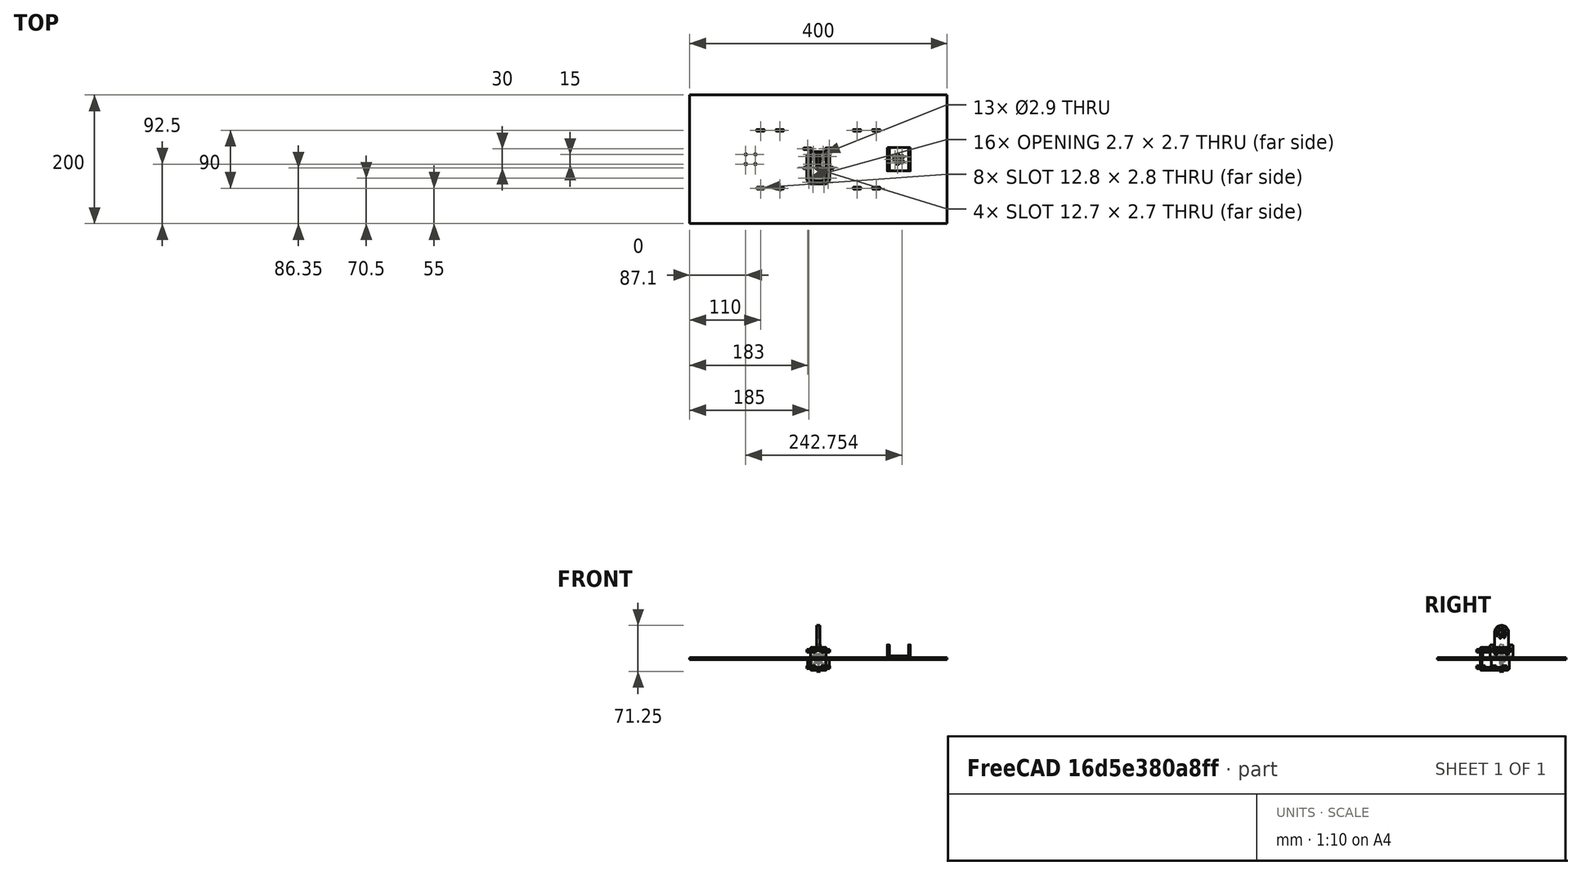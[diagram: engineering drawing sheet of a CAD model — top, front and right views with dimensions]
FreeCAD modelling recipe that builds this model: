
FCSTD DOCUMENT  (FreeCAD 1.1R20260414 (Git shallow))
Label: Unnamed
License: All rights reserved
LicenseURL: https://en.wikipedia.org/wiki/All_rights_reserved
objects: Sketcher::SketchObject×15, App::Point×8, App::Link×8, App::FeaturePython×8, PartDesign::Hole×7, Part::Feature×7, PartDesign::Pad×6, App::Part×4, PartDesign::Mirrored×3, PartDesign::Fillet×3, PartDesign::Body×3, PartDesign::Pocket×2, PartDesign::PolarPattern×2, TechDraw::DrawViewDimension×2, PartDesign::ShapeBinder×1, Assembly::JointGroup×1, Assembly::AssemblyObject×1, TechDraw::DrawSVGTemplate×1, TechDraw::DrawProjGroupItem×1, TechDraw::DrawPage×1
note: 107 computed .brp shape members not serialized (recipe doc carries the construction recipe); baked Part::Feature solids carry a one-line shape summary decoded from their .brp
EXTERNAL_REF file=Unnamed1.FCStd obj=Body

FEATURE [App::Point] Origin001
  Role = Origin
FEATURE [Sketcher::SketchObject] Sketch
  ArcFitTolerance = 1e-06
  AttachmentSupport = -> [Origin]
  ExternalTypes = [0]
  FullyConstrained = true
  MakeInternals = false
  MapMode = 5
  _ExternalGeoVersion = 1
  sketch-geometry (5):
    g0: LineSegment StartX=-200 StartY=-100 StartZ=0 EndX=200 EndY=-100 EndZ=0
    g1: LineSegment StartX=200 StartY=-100 StartZ=0 EndX=200 EndY=100 EndZ=0
    g2: LineSegment StartX=200 StartY=100 StartZ=0 EndX=-200 EndY=100 EndZ=0
    g3: LineSegment StartX=-200 StartY=100 StartZ=0 EndX=-200 EndY=-100 EndZ=0
    g4: GeomPoint [constr] X=0 Y=0 Z=0
  constraints (12):
    c: Coincident(g0,g1)
    c: Coincident(g1,g2)
    c: Coincident(g2,g3)
    c: Coincident(g3,g0)
    c: Horizontal(g0)
    c: Horizontal(g2)
    c: Vertical(g1)
    c: Vertical(g3)
    c: Symmetric(g2,g0,g4)
    c: Distance(g1,g3) = 400
    c: Distance(g0,g2) = 200
    c: Coincident(g4,g-1)
FEATURE [PartDesign::Pad] Pad
  Direction = (0,0,1)
  Length = 3
  Length2 = 10
  Profile = -> Sketch
  ReferenceAxis = -> Sketch [N_Axis]
  Refine = true
  SideType = 0
  Suppressed = false
  Type = 0
  Type2 = 0
FEATURE [Sketcher::SketchObject] Sketch001
  ArcFitTolerance = 1e-06
  AttachmentSupport = -> [Pad]
  ExternalTypes = [0]
  FullyConstrained = true
  MakeInternals = false
  MapMode = 5
  Placement = pos=(0,0,3) rot=(0,0,1;0rad)
  _ExternalGeoVersion = 1
  sketch-geometry (16):
    g0: ArcOfCircle CenterX=-12 CenterY=16.35 CenterZ=0 NormalX=0 NormalY=0 NormalZ=1 AngleXU=0 Radius=1.35 StartAngle=4.71239 EndAngle=7.85398
    g1: ArcOfCircle CenterX=-22 CenterY=16.35 CenterZ=0 NormalX=0 NormalY=0 NormalZ=1 AngleXU=0 Radius=1.35 StartAngle=1.5708 EndAngle=4.71239
    g2: LineSegment StartX=-12 StartY=15 StartZ=0 EndX=-22 EndY=15 EndZ=0
    g3: LineSegment StartX=-12 StartY=17.7 StartZ=0 EndX=-22 EndY=17.7 EndZ=0
    g4: ArcOfCircle CenterX=12 CenterY=16.35 CenterZ=0 NormalX=0 NormalY=0 NormalZ=1 AngleXU=0 Radius=1.35 StartAngle=1.5708 EndAngle=4.71239
    g5: ArcOfCircle CenterX=22 CenterY=16.35 CenterZ=0 NormalX=0 NormalY=0 NormalZ=1 AngleXU=0 Radius=1.35 StartAngle=4.71239 EndAngle=7.85398
    g6: LineSegment StartX=12 StartY=17.7 StartZ=0 EndX=22 EndY=17.7 EndZ=0
    g7: LineSegment StartX=12 StartY=15 StartZ=0 EndX=22 EndY=15 EndZ=0
    g8: ArcOfCircle CenterX=-22 CenterY=-13.65 CenterZ=0 NormalX=0 NormalY=0 NormalZ=1 AngleXU=0 Radius=1.35 StartAngle=1.5708 EndAngle=4.71239
    g9: ArcOfCircle CenterX=-12 CenterY=-13.65 CenterZ=0 NormalX=0 NormalY=0 NormalZ=1 AngleXU=0 Radius=1.35 StartAngle=4.71239 EndAngle=7.85398
    g10: LineSegment StartX=-22 StartY=-12.3 StartZ=0 EndX=-12 EndY=-12.3 EndZ=0
    g11: LineSegment StartX=-22 StartY=-15 StartZ=0 EndX=-12 EndY=-15 EndZ=0
    g12: ArcOfCircle CenterX=12 CenterY=-13.65 CenterZ=0 NormalX=0 NormalY=0 NormalZ=1 AngleXU=0 Radius=1.35 StartAngle=1.5708 EndAngle=4.71239
    g13: ArcOfCircle CenterX=22 CenterY=-13.65 CenterZ=0 NormalX=0 NormalY=0 NormalZ=1 AngleXU=0 Radius=1.35 StartAngle=4.71239 EndAngle=7.85398
    g14: LineSegment StartX=12 StartY=-12.3 StartZ=0 EndX=22 EndY=-12.3 EndZ=0
    g15: LineSegment StartX=12 StartY=-15 StartZ=0 EndX=22 EndY=-15 EndZ=0
  constraints (40):
    c: Tangent(g0,g2) = 1.5708
    c: Tangent(g0,g3) = -1.5708
    c: Tangent(g1,g2) = 1.5708
    c: Tangent(g1,g3) = -1.5708
    c: Equal(g0,g1)
    c: Distance(g0,g1) = 10
    c: Radius(g0) = 1.35
    c: Horizontal(g2)
    c: Distance(g0,g-2) = 12
    c: Tangent(g4,g6) = 1.5708
    c: Tangent(g4,g7) = -1.5708
    c: Tangent(g5,g6) = 1.5708
    c: Tangent(g5,g7) = -1.5708
    c: Equal(g4,g5)
    c: Distance(g4,g5) = 10
    c: Radius(g4) = 1.35
    c: Horizontal(g6)
    c: Distance(g4,g-2) = 12
    c: Distance(g-1,g7) = 15
    c: Distance(g-1,g2) = 15
    c: Tangent(g8,g10) = 1.5708
    c: Tangent(g8,g11) = -1.5708
    c: Tangent(g9,g10) = 1.5708
    c: Tangent(g9,g11) = -1.5708
    c: Equal(g8,g9)
    c: Distance(g8,g9) = 10
    c: Radius(g8) = 1.35
    c: Horizontal(g10)
    c: Distance(g9,g-2) = 12
    c: DistanceY(g9,g0) = 30
    c: Tangent(g12,g14) = 1.5708
    c: Tangent(g12,g15) = -1.5708
    c: Tangent(g13,g14) = 1.5708
    c: Tangent(g13,g15) = -1.5708
    c: Equal(g12,g13)
    c: Distance(g12,g13) = 10
    c: Radius(g12) = 1.35
    c: Horizontal(g14)
    c: Distance(g12,g-2) = 12
    c: Distance(g12,g4) = 30
FEATURE [PartDesign::Pocket] Pocket
  BaseFeature = -> Pad
  Direction = (0,0,-1)
  Length = 5
  Length2 = 5
  Profile = -> Sketch001
  ReferenceAxis = -> Sketch001 [N_Axis]
  Refine = true
  SideType = 0
  Suppressed = false
  Type = 0
  Type2 = 0
FEATURE [Sketcher::SketchObject] Sketch002
  ArcFitTolerance = 1e-06
  AttachmentSupport = -> [Pocket]
  ExternalTypes = [0]
  FullyConstrained = true
  MakeInternals = false
  MapMode = 5
  Placement = pos=(0,0,3) rot=(0,0,1;0rad)
  _ExternalGeoVersion = 1
  sketch-geometry (8):
    g0: ArcOfCircle CenterX=-55 CenterY=-45 CenterZ=0 NormalX=0 NormalY=0 NormalZ=1 AngleXU=0 Radius=1.4 StartAngle=4.71239 EndAngle=7.85398
    g1: ArcOfCircle CenterX=-65 CenterY=-45 CenterZ=0 NormalX=0 NormalY=0 NormalZ=1 AngleXU=0 Radius=1.4 StartAngle=1.5708 EndAngle=4.71239
    g2: LineSegment StartX=-55 StartY=-46.4 StartZ=0 EndX=-65 EndY=-46.4 EndZ=0
    g3: LineSegment StartX=-55 StartY=-43.6 StartZ=0 EndX=-65 EndY=-43.6 EndZ=0
    g4: ArcOfCircle CenterX=-85 CenterY=-45 CenterZ=0 NormalX=0 NormalY=0 NormalZ=1 AngleXU=0 Radius=1.4 StartAngle=4.71239 EndAngle=7.85398
    g5: ArcOfCircle CenterX=-95 CenterY=-45 CenterZ=0 NormalX=0 NormalY=0 NormalZ=1 AngleXU=0 Radius=1.4 StartAngle=1.5708 EndAngle=4.71239
    g6: LineSegment StartX=-85 StartY=-46.4 StartZ=0 EndX=-95 EndY=-46.4 EndZ=0
    g7: LineSegment StartX=-85 StartY=-43.6 StartZ=0 EndX=-95 EndY=-43.6 EndZ=0
  constraints (20):
    c: Tangent(g0,g2) = 1.5708
    c: Tangent(g0,g3) = -1.5708
    c: Tangent(g1,g2) = 1.5708
    c: Tangent(g1,g3) = -1.5708
    c: Equal(g0,g1)
    c: Distance(g0,g1) = 10
    c: Radius(g0) = 1.4
    c: Horizontal(g2)
    c: Distance(g0,g-2) = 55
    c: Distance(g0,g-1) = 45
    c: Tangent(g4,g6) = 1.5708
    c: Tangent(g4,g7) = -1.5708
    c: Tangent(g5,g6) = 1.5708
    c: Tangent(g5,g7) = -1.5708
    c: Equal(g4,g5)
    c: Distance(g4,g5) = 10
    c: Radius(g4) = 1.4
    c: Horizontal(g6)
    c: DistanceX(g4,g1) = 20
    c: Distance(g5,g-1) = 45
FEATURE [PartDesign::Pocket] Pocket001
  BaseFeature = -> Pocket
  Direction = (0,0,-1)
  Length = 5
  Length2 = 5
  Profile = -> Sketch002
  ReferenceAxis = -> Sketch002 [N_Axis]
  Refine = true
  SideType = 0
  Suppressed = false
  Type = 0
  Type2 = 0
FEATURE [PartDesign::Mirrored] Mirrored
  BaseFeature = -> Pocket001
  MirrorPlane = -> Sketch002 [V_Axis]
  Originals = -> [Pocket001]
  Refine = true
  Suppressed = false
  TransformMode = 0
FEATURE [PartDesign::Mirrored] Mirrored001
  BaseFeature = -> Mirrored
  MirrorPlane = -> Sketch002 [H_Axis]
  Originals = -> [Pocket001]
  Refine = true
  Suppressed = false
  TransformMode = 0
FEATURE [PartDesign::PolarPattern] PolarPattern
  Angle = 360
  Axis = -> Sketch002 [N_Axis]
  BaseFeature = -> Mirrored001
  Mode = 0
  Occurrences = 2
  Offset = 120
  Originals = -> [Pocket001]
  Refine = true
  SpacingPattern = [0]
  Spacings = [-1]
  Suppressed = false
  TransformMode = 0
FEATURE [PartDesign::ShapeBinder] CopyPart__Feature
  TraceSupport = false
FEATURE [Sketcher::SketchObject] Sketch003
  ArcFitTolerance = 1e-06
  AttachmentSupport = -> [CopyPart__Feature]
  ExternalTypes = [0]
  FullyConstrained = true
  MakeInternals = false
  MapMode = 5
  Placement = pos=(0,-38.6,0) rot=(1,0,0;1.5708rad)
  _ExternalGeoVersion = 1
  sketch-geometry (5):
    g0: LineSegment StartX=-18 StartY=-15 StartZ=0 EndX=18 EndY=-15 EndZ=0
    g1: LineSegment StartX=18 StartY=-15 StartZ=0 EndX=18 EndY=15 EndZ=0
    g2: LineSegment StartX=18 StartY=15 StartZ=0 EndX=-18 EndY=15 EndZ=0
    g3: LineSegment StartX=-18 StartY=15 StartZ=0 EndX=-18 EndY=-15 EndZ=0
    g4: GeomPoint [constr] X=0 Y=0 Z=0
  constraints (12):
    c: Coincident(g0,g1)
    c: Coincident(g1,g2)
    c: Coincident(g2,g3)
    c: Coincident(g3,g0)
    c: Horizontal(g0)
    c: Horizontal(g2)
    c: Vertical(g1)
    c: Vertical(g3)
    c: Symmetric(g2,g0,g4)
    c: Distance(g1,g3) = 36
    c: Distance(g0,g2) = 30
    c: Coincident(g4,g-1)
FEATURE [PartDesign::Pad] Pad001
  Direction = (0,-1,2e-16)
  Length = 3
  Length2 = 10
  Profile = -> Sketch003
  ReferenceAxis = -> Sketch003 [N_Axis]
  Refine = true
  SideType = 0
  Suppressed = false
  Type = 0
  Type2 = 0
FEATURE [Sketcher::SketchObject] Sketch004
  ArcFitTolerance = 1e-06
  AttachmentSupport = -> [Pad001]
  ExternalTypes = [0]
  FullyConstrained = true
  MakeInternals = false
  MapMode = 5
  Placement = pos=(0,3.3e-15,15) rot=(0,0,1;0rad)
  _ExternalGeoVersion = 1
  sketch-geometry (12):
    g0: LineSegment StartX=-18 StartY=-21.6 StartZ=0 EndX=-12.5 EndY=-21.6 EndZ=0
    g1: LineSegment StartX=-12.5 StartY=-21.6 StartZ=0 EndX=-12.5 EndY=-33.6 EndZ=0
    g2: LineSegment StartX=-12.5 StartY=-33.6 StartZ=0 EndX=12.5 EndY=-33.6 EndZ=0
    g3: LineSegment StartX=12.5 StartY=-33.6 StartZ=0 EndX=12.5 EndY=-21.6 EndZ=0
    g4: LineSegment StartX=12.5 StartY=-21.6 StartZ=0 EndX=18 EndY=-21.6 EndZ=0
    g5: LineSegment StartX=18 StartY=-21.6 StartZ=0 EndX=18 EndY=-41.6 EndZ=0
    g6: LineSegment StartX=18 StartY=-41.6 StartZ=0 EndX=-18 EndY=-41.6 EndZ=0
    g7: LineSegment StartX=-18 StartY=-41.6 StartZ=0 EndX=-18 EndY=-21.6 EndZ=0
    g8: Circle CenterX=-15 CenterY=-29.5 CenterZ=0 NormalX=0 NormalY=0 NormalZ=1 AngleXU=0 Radius=1.5
    g9: Circle CenterX=-8.5 CenterY=-35.8 CenterZ=0 NormalX=0 NormalY=0 NormalZ=1 AngleXU=0 Radius=1.5
    g10: Circle CenterX=8.5 CenterY=-35.8 CenterZ=0 NormalX=0 NormalY=0 NormalZ=1 AngleXU=0 Radius=1.5
    g11: Circle CenterX=15 CenterY=-29.5 CenterZ=0 NormalX=0 NormalY=0 NormalZ=1 AngleXU=0 Radius=1.5
  constraints (36):
    c: Horizontal(g0)
    c: Coincident(g0,g1)
    c: Vertical(g1)
    c: Coincident(g1,g2)
    c: Horizontal(g2)
    c: Coincident(g2,g3)
    c: Vertical(g3)
    c: Coincident(g3,g4)
    c: Horizontal(g4)
    c: Coincident(g4,g5)
    c: Vertical(g5)
    c: Coincident(g5,g6)
    c: Horizontal(g6)
    c: Coincident(g6,g7)
    c: Coincident(g7,g0)
    c: Vertical(g7)
    c: DistanceX(g6,g6) = 36
    c: DistanceY(g7,g7) = 20
    c: Distance(g3,g1) = 25
    c: Equal(g0,g4)
    c: Equal(g3,g1)
    c: Distance(g-1,g6) = 41.6
    c: Distance(g-2,g7) = 18
    c: Distance(g6,g2) = 8
    c: Diameter(g8) = 3
    c: Equal(g8,g9)
    c: Equal(g9,g10)
    c: Equal(g10,g11)
    c: Distance(g8,g7) = 3
    c: Distance(g9,g6) = 5.8
    c: Distance(g9,g7) = 9.5
    c: Distance(g10,g5) = 9.5
    c: Distance(g10,g6) = 5.8
    c: Distance(g11,g5) = 3
    c: Distance(g8,g0) = 7.9
    c: Distance(g11,g4) = 7.9
FEATURE [PartDesign::Pad] Pad002
  BaseFeature = -> Pad001
  Direction = (0,0,1)
  Length = 3
  Length2 = 10
  Profile = -> Sketch004
  ReferenceAxis = -> Sketch004 [N_Axis]
  Refine = true
  SideType = 0
  Suppressed = false
  Type = 0
  Type2 = 0
FEATURE [PartDesign::Mirrored] Mirrored002
  BaseFeature = -> Pad002
  MirrorPlane = -> XY_Plane001
  Originals = -> [Pad002]
  Refine = true
  Suppressed = false
  TransformMode = 0
FEATURE [PartDesign::Fillet] Fillet001
  Base = -> Mirrored002 [Edge60,Edge47,Edge36,Edge27]
  BaseFeature = -> Mirrored002
  Radius = 2
  Refine = true
  SupportTransform = false
  Suppressed = false
  UseAllEdges = false
FEATURE [PartDesign::Fillet] Fillet002
  Base = -> Fillet001 [Edge51,Edge56]
  BaseFeature = -> Fillet001
  Radius = 1
  Refine = true
  SupportTransform = false
  Suppressed = false
  UseAllEdges = false
FEATURE [Sketcher::SketchObject] Sketch005
  ArcFitTolerance = 1e-06
  AttachmentSupport = -> [Fillet002]
  ExternalTypes = [0]
  FullyConstrained = true
  MakeInternals = false
  MapMode = 5
  Placement = pos=(0,-38.6,0) rot=(0,0.707107,0.707107;3.14159rad)
  _ExternalGeoVersion = 1
  sketch-geometry (1):
    g0: Circle CenterX=0 CenterY=6 CenterZ=0 NormalX=0 NormalY=0 NormalZ=1 AngleXU=0 Radius=1.25
  constraints (3):
    c: Diameter(g0) = 2.5
    c: PointOnObject(g0,g-2)
    c: Distance(g0,g-1) = 6
FEATURE [PartDesign::Hole] Hole
  BaseFeature = -> Fillet002
  BaseProfileType = 7
  CustomThreadClearance = 0
  Depth = 5
  DepthType = 0
  Diameter = 2.9
  DrillForDepth = false
  DrillPoint = 1
  DrillPointAngle = 118
  HoleCutCountersinkAngle = 90
  HoleCutCustomValues = false
  HoleCutDepth = 2.65
  HoleCutDiameter = 5.3
  HoleCutType = 7
  ModelThread = false
  Profile = -> Sketch005
  Refine = true
  Suppressed = false
  Tapered = false
  TaperedAngle = 90
  ThreadClass = 0
  ThreadDepth = 5
  ThreadDepthType = 0
  ThreadDiameter = 2.5
  ThreadDirection = 0
  ThreadFit = 0
  ThreadSize = 8
  ThreadType = 1
  Threaded = false
  UseCustomThreadClearance = false
FEATURE [PartDesign::PolarPattern] PolarPattern001
  Angle = 360
  Axis = -> Sketch005 [N_Axis]
  BaseFeature = -> Hole
  Mode = 0
  Occurrences = 5
  Offset = 120
  Originals = -> [Hole]
  Refine = true
  SpacingPattern = [0]
  Spacings = [-1,-1,-1,-1]
  Suppressed = false
  TransformMode = 0
FEATURE [App::Point] Origin003
  Role = Origin
FEATURE [PartDesign::Body] Body001  label="mx_28_holder"
  AllowCompound = true
  Group = -> [CopyPart__Feature,Sketch003,Pad001,Sketch004,Pad002,Mirrored002,Fillet001,Fillet002,Sketch005,Hole,PolarPattern001]
  Origin = -> Origin002
  Placement = pos=(125,5.4e-15,44.5) rot=(-0.57735,0.57735,0.57735;4.18879rad)
  Tip = -> PolarPattern001
FEATURE [App::Point] Origin006  label="Origin008"
  Role = Origin
FEATURE [Part::Feature] Part__Feature  label="DC07_00A_DUMMY_NONE"
  Placement = pos=(0,0,1) rot=(0,0,1;0rad)
  shape: bbox 35.6 x 51.12 x 41.85 mm, 333 faces (baked)
FEATURE [App::Point] Origin008  label="Origin010"
  Role = Origin
FEATURE [Part::Feature] Part__Feature001  label="SOLID001"
  shape: bbox 22 x 3.05 x 22 mm, 56 faces (baked)
FEATURE [Part::Feature] Part__Feature002  label="COMPOUND001"
  shape: bbox 18 x 1.95 x 18 mm, 16 faces, 0 solids (baked)
FEATURE [App::Part] HN07_I_02
  Group = -> [Part__Feature001,Part__Feature002]
  Origin = -> Origin009
  Placement = pos=(2e-16,0,-19.15) rot=(-0.672416,0.523382,-0.523382;1.95765rad)
FEATURE [App::Point] Origin010  label="Origin012"
  Role = Origin
FEATURE [Part::Feature] Part__Feature003  label="SOLID"
  shape: bbox 22 x 5.851 x 22 mm, 149 faces (baked)
FEATURE [Part::Feature] Part__Feature004  label="COMPOUND"
  shape: bbox 18 x 1.95 x 18 mm, 16 faces, 0 solids (baked)
FEATURE [App::Part] HN07_N_02
  Group = -> [Part__Feature003,Part__Feature004]
  Origin = -> Origin011
  Placement = pos=(0,0,19.3) rot=(0.57735,0.57735,0.57735;2.0944rad)
FEATURE [App::Part] Unnamed  label="mx28"
  Group = -> [Part__Feature,HN07_I_02,HN07_N_02]
  Origin = -> Origin007
  Placement = pos=(126,-4.25e-14,45) rot=(0.57735,-0.57735,-0.57735;2.0944rad)
FEATURE [Sketcher::SketchObject] Sketch006
  ArcFitTolerance = 1e-06
  AttachmentSupport = -> [PolarPattern]
  ExternalTypes = [0]
  FullyConstrained = true
  MakeInternals = false
  MapMode = 5
  Placement = pos=(0,0,3) rot=(0,0,1;0rad)
  _ExternalGeoVersion = 1
  sketch-geometry (5):
    g0: Circle CenterX=123.15 CenterY=5.7 CenterZ=0 NormalX=0 NormalY=0 NormalZ=1 AngleXU=0 Radius=1.25
    g1: Circle CenterX=119 CenterY=0 CenterZ=0 NormalX=0 NormalY=0 NormalZ=1 AngleXU=0 Radius=1.25
    g2: Circle CenterX=129.85 CenterY=3.55 CenterZ=0 NormalX=0 NormalY=0 NormalZ=1 AngleXU=0 Radius=1.25
    g3: Circle CenterX=123.15 CenterY=-5.7 CenterZ=0 NormalX=0 NormalY=0 NormalZ=1 AngleXU=0 Radius=1.25
    g4: Circle CenterX=129.85 CenterY=-3.52 CenterZ=0 NormalX=0 NormalY=0 NormalZ=1 AngleXU=0 Radius=1.25
  constraints (15):
    c: Diameter(g0) = 2.5
    c: PointOnObject(g1,g-1)
    c: Equal(g1,g0)
    c: Equal(g1,g3)
    c: Equal(g3,g4)
    c: Equal(g4,g2)
    c: DistanceX(g-1,g0) = 123.15
    c: DistanceX(g-1,g1) = 119
    c: DistanceX(g-1,g3) = 123.15
    c: DistanceX(g-1,g4) = 129.85
    c: DistanceX(g-1,g2) = 129.85
    c: Distance(g0,g-1) = 5.7
    c: Distance(g2,g-1) = 3.55
    c: Distance(g4,g-1) = 3.52
    c: Distance(g3,g-1) = 5.7
FEATURE [PartDesign::Hole] Hole001
  BaseFeature = -> PolarPattern
  BaseProfileType = 7
  CustomThreadClearance = 0
  Depth = 5
  DepthType = 0
  Diameter = 3.1
  DrillForDepth = false
  DrillPoint = 1
  DrillPointAngle = 118
  HoleCutCountersinkAngle = 90
  HoleCutCustomValues = false
  HoleCutDepth = 0
  HoleCutDiameter = 0
  HoleCutType = 0
  ModelThread = false
  Profile = -> Sketch006
  Refine = true
  Suppressed = false
  Tapered = false
  TaperedAngle = 90
  ThreadClass = 0
  ThreadDepth = 5
  ThreadDepthType = 0
  ThreadDiameter = 2.5
  ThreadDirection = 0
  ThreadFit = 2
  ThreadSize = 8
  ThreadType = 1
  Threaded = false
  UseCustomThreadClearance = false
FEATURE [Sketcher::SketchObject] Sketch011
  ArcFitTolerance = 1e-06
  AttachmentSupport = -> [Hole001]
  ExternalTypes = [0]
  FullyConstrained = true
  MakeInternals = false
  MapMode = 5
  Placement = pos=(0,0,3) rot=(0,0,1;0rad)
  _ExternalGeoVersion = 1
  sketch-geometry (5):
    g0: GeomPoint [constr] X=-105.4 Y=0 Z=0
    g1: Circle CenterX=-97.9 CenterY=7.49998 CenterZ=0 NormalX=0 NormalY=0 NormalZ=1 AngleXU=0 Radius=1.1
    g2: Circle CenterX=-112.9 CenterY=7.50002 CenterZ=0 NormalX=0 NormalY=0 NormalZ=1 AngleXU=0 Radius=1.1
    g3: Circle CenterX=-112.9 CenterY=-7.49998 CenterZ=0 NormalX=0 NormalY=0 NormalZ=1 AngleXU=0 Radius=1.1
    g4: Circle CenterX=-97.9 CenterY=-7.50002 CenterZ=0 NormalX=0 NormalY=0 NormalZ=1 AngleXU=0 Radius=1.1
  constraints (13):
    c: PointOnObject(g0,g-1)
    c: Symmetric(g1,g3,g0)
    c: Distance(g4,g3) = 15
    c: Distance(g3,g2) = 15
    c: Diameter(g1) = 2.2
    c: Equal(g1,g2)
    c: Equal(g2,g3)
    c: Equal(g3,g4)
    c: DistanceX(g1,g-1) = 97.9
    c: Distance(g1,g4) = 15
    c: DistanceX(g2,g1) = 15
    c: DistanceX(g3,g-1) = 112.9
    c: DistanceX(g4,g-1) = 97.9
FEATURE [PartDesign::Hole] Hole004
  BaseFeature = -> Hole001
  BaseProfileType = 7
  CustomThreadClearance = 0
  Depth = 5
  DepthType = 0
  Diameter = 2.9
  DrillForDepth = false
  DrillPoint = 1
  DrillPointAngle = 118
  HoleCutCountersinkAngle = 90
  HoleCutCustomValues = false
  HoleCutDepth = 0
  HoleCutDiameter = 0
  HoleCutType = 0
  ModelThread = false
  Profile = -> Sketch011
  Refine = true
  Suppressed = false
  Tapered = false
  TaperedAngle = 90
  ThreadClass = 0
  ThreadDepth = 5
  ThreadDepthType = 0
  ThreadDiameter = 2.5
  ThreadDirection = 0
  ThreadFit = 0
  ThreadSize = 8
  ThreadType = 1
  Threaded = false
  UseCustomThreadClearance = false
FEATURE [PartDesign::Body] Body  label="base"
  AllowCompound = true
  Group = -> [Sketch,Pad,Sketch001,Pocket,Sketch002,Pocket001,Mirrored,Mirrored001,PolarPattern,Sketch006,Hole001,Sketch011,Hole004]
  Origin = -> Origin
  Tip = -> Hole004
FEATURE [App::Point] Origin014  label="Origin016"
  Role = Origin
FEATURE [Part::Feature] Part__Feature005  label="SOLID002"
  shape: bbox 22 x 3.05 x 22 mm, 56 faces (baked)
FEATURE [Part::Feature] Part__Feature006  label="COMPOUND002"
  shape: bbox 18 x 1.95 x 18 mm, 16 faces, 0 solids (baked)
FEATURE [App::Part] HN07_I_001
  Group = -> [Part__Feature005,Part__Feature006]
  Origin = -> Origin015
  Placement = pos=(-102.51,0.0161296,44.95) rot=(-0.702206,0.711974,0;3.14159rad)
FEATURE [App::Point] Origin012  label="Origin014"
  Role = Origin
FEATURE [Sketcher::SketchObject] Sketch012
  ArcFitTolerance = 1e-06
  AttachmentSupport = -> [Origin013]
  ExternalTypes = [0]
  FullyConstrained = true
  MakeInternals = false
  MapMode = 5
  _ExternalGeoVersion = 1
  sketch-geometry (5):
    g0: LineSegment StartX=-12 StartY=-12 StartZ=0 EndX=12 EndY=-12 EndZ=0
    g1: LineSegment StartX=12 StartY=-12 StartZ=0 EndX=12 EndY=12 EndZ=0
    g2: LineSegment StartX=12 StartY=12 StartZ=0 EndX=-12 EndY=12 EndZ=0
    g3: LineSegment StartX=-12 StartY=12 StartZ=0 EndX=-12 EndY=-12 EndZ=0
    g4: GeomPoint [constr] X=0 Y=0 Z=0
  constraints (12):
    c: Coincident(g0,g1)
    c: Coincident(g1,g2)
    c: Coincident(g2,g3)
    c: Coincident(g3,g0)
    c: Horizontal(g0)
    c: Horizontal(g2)
    c: Vertical(g1)
    c: Vertical(g3)
    c: Symmetric(g2,g0,g4)
    c: Distance(g1,g3) = 24
    c: Distance(g0,g2) = 24
    c: Coincident(g4,g-1)
FEATURE [PartDesign::Pad] Pad003
  Direction = (0,0,1)
  Length = 5
  Length2 = 10
  Profile = -> Sketch012
  ReferenceAxis = -> Sketch012 [N_Axis]
  Refine = true
  SideType = 0
  Suppressed = false
  Type = 0
  Type2 = 0
FEATURE [Sketcher::SketchObject] Sketch013
  ArcFitTolerance = 1e-06
  AttachmentSupport = -> [Pad003]
  ExternalTypes = [0]
  FullyConstrained = true
  MakeInternals = false
  MapMode = 5
  Placement = pos=(0,0,5) rot=(0,0,1;0rad)
  _ExternalGeoVersion = 1
  sketch-geometry (5):
    g0: GeomPoint [constr] X=0 Y=0 Z=0
    g1: Circle CenterX=7.5 CenterY=7.5 CenterZ=0 NormalX=0 NormalY=0 NormalZ=1 AngleXU=0 Radius=1.1
    g2: Circle CenterX=-7.5 CenterY=7.5 CenterZ=0 NormalX=0 NormalY=0 NormalZ=1 AngleXU=0 Radius=1.1
    g3: Circle CenterX=-7.5 CenterY=-7.5 CenterZ=0 NormalX=0 NormalY=0 NormalZ=1 AngleXU=0 Radius=1.1
    g4: Circle CenterX=7.5 CenterY=-7.5 CenterZ=0 NormalX=0 NormalY=0 NormalZ=1 AngleXU=0 Radius=1.1
  constraints (12):
    c: Symmetric(g1,g3,g0)
    c: Distance(g4,g3) = 15
    c: Distance(g3,g2) = 15
    c: Coincident(g0,g-1)
    c: Diameter(g1) = 2.2
    c: Equal(g1,g2)
    c: Equal(g2,g3)
    c: Equal(g3,g4)
    c: DistanceX(g2,g1) = 15
    c: DistanceY(g4,g1) = 15
    c: Distance(g4,g-2) = 7.5
    c: Distance(g2,g-1) = 7.5
FEATURE [PartDesign::Hole] Hole005
  BaseFeature = -> Pad003
  BaseProfileType = 7
  CustomThreadClearance = 0
  Depth = 5
  DepthType = 0
  Diameter = 2.9
  DrillForDepth = false
  DrillPoint = 1
  DrillPointAngle = 118
  HoleCutCountersinkAngle = 90
  HoleCutCustomValues = false
  HoleCutDepth = 0
  HoleCutDiameter = 0
  HoleCutType = 0
  ModelThread = false
  Profile = -> Sketch013
  Refine = true
  Suppressed = false
  Tapered = false
  TaperedAngle = 90
  ThreadClass = 0
  ThreadDepth = 5
  ThreadDepthType = 0
  ThreadDiameter = 2.5
  ThreadDirection = 0
  ThreadFit = 0
  ThreadSize = 8
  ThreadType = 1
  Threaded = false
  UseCustomThreadClearance = false
FEATURE [Sketcher::SketchObject] Sketch014
  ArcFitTolerance = 1e-06
  AttachmentSupport = -> [Hole005]
  ExternalTypes = [0]
  FullyConstrained = true
  MakeInternals = false
  MapMode = 5
  Placement = pos=(0,0,5) rot=(0,0,1;0rad)
  _ExternalGeoVersion = 1
  sketch-geometry (5):
    g0: LineSegment StartX=-2.5 StartY=-11 StartZ=0 EndX=2.5 EndY=-11 EndZ=0
    g1: LineSegment StartX=2.5 StartY=-11 StartZ=0 EndX=2.5 EndY=11 EndZ=0
    g2: LineSegment StartX=2.5 StartY=11 StartZ=0 EndX=-2.5 EndY=11 EndZ=0
    g3: LineSegment StartX=-2.5 StartY=11 StartZ=0 EndX=-2.5 EndY=-11 EndZ=0
    g4: GeomPoint [constr] X=0 Y=0 Z=0
  constraints (12):
    c: Coincident(g0,g1)
    c: Coincident(g1,g2)
    c: Coincident(g2,g3)
    c: Coincident(g3,g0)
    c: Horizontal(g0)
    c: Horizontal(g2)
    c: Vertical(g1)
    c: Vertical(g3)
    c: Symmetric(g2,g0,g4)
    c: Distance(g1,g3) = 5
    c: Distance(g0,g2) = 22
    c: Coincident(g4,g-1)
FEATURE [PartDesign::Pad] Pad004
  BaseFeature = -> Hole005
  Direction = (0,0,1)
  Length = 37
  Length2 = 10
  Profile = -> Sketch014
  ReferenceAxis = -> Sketch014 [N_Axis]
  Refine = true
  SideType = 0
  Suppressed = false
  Type = 0
  Type2 = 0
FEATURE [PartDesign::Fillet] Fillet
  Base = -> Pad004 [Edge23,Edge21]
  BaseFeature = -> Pad004
  Radius = 3
  Refine = true
  SupportTransform = false
  Suppressed = false
  UseAllEdges = false
FEATURE [Sketcher::SketchObject] Sketch015
  ArcFitTolerance = 1e-06
  AttachmentSupport = -> [Fillet]
  ExternalTypes = [0,0]
  FullyConstrained = true
  MakeInternals = false
  MapMode = 5
  Placement = pos=(-2.5,0,0) rot=(0.57735,-0.57735,-0.57735;2.0944rad)
  _ExternalGeoVersion = 1
  sketch-geometry (2):
    g0: ArcOfCircle CenterX=6.6e-13 CenterY=42 CenterZ=0 NormalX=0 NormalY=0 NormalZ=1 AngleXU=0 Radius=11 StartAngle=0 EndAngle=3.14159
    g1: LineSegment StartX=-11 StartY=42 StartZ=0 EndX=11 EndY=42 EndZ=0
  constraints (7):
    c: Coincident(g1,g0)
    c: Coincident(g1,g0)
    c: DistanceY(g-1,g0) = 42
    c: DistanceY(g-1,g0) = 42
    c: Distance(g0,g-2) = 11
    c: Distance(g0,g-2) = 11
    c: Distance(g0,g-1) = 31
FEATURE [PartDesign::Pad] Pad005
  BaseFeature = -> Fillet
  Direction = (-1,0,0)
  Length = 5
  Length2 = 10
  Profile = -> Sketch015
  ReferenceAxis = -> Sketch015 [N_Axis]
  Refine = true
  Reversed = true
  SideType = 0
  Suppressed = false
  Type = 0
  Type2 = 0
FEATURE [Sketcher::SketchObject] Sketch016
  ArcFitTolerance = 1e-06
  AttachmentSupport = -> [Pad005]
  ExternalTypes = [0]
  FullyConstrained = true
  MakeInternals = false
  MapMode = 5
  Placement = pos=(2.5,0,0) rot=(0.57735,0.57735,0.57735;2.0944rad)
  _ExternalGeoVersion = 1
  sketch-geometry (8):
    g0: Circle CenterX=-6.87 CenterY=37.91 CenterZ=0 NormalX=0 NormalY=0 NormalZ=1 AngleXU=0 Radius=0.75
    g1: Circle CenterX=-7.75 CenterY=43.96 CenterZ=0 NormalX=0 NormalY=0 NormalZ=1 AngleXU=0 Radius=0.75
    g2: Circle CenterX=-4.1 CenterY=48.87 CenterZ=0 NormalX=0 NormalY=0 NormalZ=1 AngleXU=0 Radius=0.75
    g3: Circle CenterX=1.96 CenterY=49.75 CenterZ=0 NormalX=0 NormalY=0 NormalZ=1 AngleXU=0 Radius=0.75
    g4: Circle CenterX=6.87 CenterY=46.09 CenterZ=0 NormalX=0 NormalY=0 NormalZ=1 AngleXU=0 Radius=0.75
    g5: Circle CenterX=7.75 CenterY=40.04 CenterZ=0 NormalX=0 NormalY=0 NormalZ=1 AngleXU=0 Radius=0.75
    g6: Circle CenterX=4.1 CenterY=35.13 CenterZ=0 NormalX=0 NormalY=0 NormalZ=1 AngleXU=0 Radius=0.75
    g7: Circle CenterX=-1.97 CenterY=34.24 CenterZ=0 NormalX=0 NormalY=0 NormalZ=1 AngleXU=0 Radius=0.75
  constraints (24):
    c: Diameter(g0) = 1.5
    c: Distance(g0,g-2) = 6.87
    c: Distance(g0,g-1) = 37.91
    c: Equal(g0,g1)
    c: Equal(g1,g2)
    c: Equal(g2,g3)
    c: Equal(g3,g4)
    c: Equal(g4,g5)
    c: Equal(g5,g6)
    c: Equal(g6,g7)
    c: Distance(g1,g-2) = 7.75
    c: Distance(g2,g-2) = 4.1
    c: Distance(g3,g-2) = 1.96
    c: Distance(g4,g-2) = 6.87
    c: Distance(g5,g-2) = 7.75
    c: Distance(g6,g-2) = 4.1
    c: Distance(g7,g-2) = 1.97
    c: Distance(g7,g-1) = 34.24
    c: DistanceY(g-1,g1) = 43.96
    c: DistanceY(g-1,g2) = 48.87
    c: DistanceY(g-1,g3) = 49.75
    c: DistanceY(g-1,g4) = 46.09
    c: DistanceY(g-1,g5) = 40.04
    c: DistanceY(g-1,g6) = 35.13
FEATURE [PartDesign::Hole] Hole006
  BaseFeature = -> Pad005
  BaseProfileType = 7
  CustomThreadClearance = 0
  Depth = 5
  DepthType = 0
  Diameter = 2.552
  DrillForDepth = false
  DrillPoint = 1
  DrillPointAngle = 118
  HoleCutCountersinkAngle = 90
  HoleCutCustomValues = false
  HoleCutDepth = 0
  HoleCutDiameter = 0
  HoleCutType = 0
  ModelThread = false
  Profile = -> Sketch016
  Refine = true
  Suppressed = false
  Tapered = false
  TaperedAngle = 90
  ThreadClass = 0
  ThreadDepth = 5
  ThreadDepthType = 0
  ThreadDiameter = 2.2
  ThreadDirection = 0
  ThreadFit = 2
  ThreadSize = 7
  ThreadType = 1
  Threaded = false
  UseCustomThreadClearance = false
FEATURE [Sketcher::SketchObject] Sketch017
  ArcFitTolerance = 1e-06
  AttachmentSupport = -> [Hole006]
  ExternalTypes = [0,0]
  FullyConstrained = true
  MakeInternals = false
  MapMode = 5
  Placement = pos=(2.5,0,0) rot=(0.57735,0.57735,0.57735;2.0944rad)
  _ExternalGeoVersion = 1
  sketch-geometry (1):
    g0: Circle CenterX=0 CenterY=42 CenterZ=0 NormalX=0 NormalY=0 NormalZ=1 AngleXU=0 Radius=5.5
  constraints (3):
    c: Diameter(g0) = 11
    c: PointOnObject(g0,g-2)
    c: DistanceY(g-1,g0) = 42
FEATURE [PartDesign::Hole] Hole002
  BaseFeature = -> Hole006
  BaseProfileType = 7
  CustomThreadClearance = 0
  Depth = 2.5
  DepthType = 0
  Diameter = 9
  DrillForDepth = false
  DrillPoint = 1
  DrillPointAngle = 118
  HoleCutCountersinkAngle = 90
  HoleCutCustomValues = false
  HoleCutDepth = 0
  HoleCutDiameter = 0
  HoleCutType = 0
  ModelThread = false
  Profile = -> Sketch017
  Refine = true
  Suppressed = false
  Tapered = false
  TaperedAngle = 90
  ThreadClass = 0
  ThreadDepth = 2.5
  ThreadDepthType = 0
  ThreadDiameter = 8
  ThreadDirection = 0
  ThreadFit = 0
  ThreadSize = 16
  ThreadType = 1
  Threaded = false
  UseCustomThreadClearance = false
FEATURE [Sketcher::SketchObject] Sketch018
  ArcFitTolerance = 1e-06
  AttachmentSupport = -> [Hole002]
  ExternalTypes = [0]
  FullyConstrained = true
  MakeInternals = false
  MapMode = 5
  Placement = pos=(-2.5,0,0) rot=(0.57735,-0.57735,-0.57735;2.0944rad)
  _ExternalGeoVersion = 1
  sketch-geometry (1):
    g0: Circle CenterX=0 CenterY=41.6 CenterZ=0 NormalX=0 NormalY=0 NormalZ=1 AngleXU=0 Radius=1.1
  constraints (3):
    c: Diameter(g0) = 2.2
    c: PointOnObject(g0,g-2)
    c: DistanceY(g-1,g0) = 41.6
FEATURE [PartDesign::Hole] Hole007
  BaseFeature = -> Hole002
  BaseProfileType = 7
  CustomThreadClearance = 0
  Depth = 2.5
  DepthType = 0
  Diameter = 2.9
  DrillForDepth = false
  DrillPoint = 1
  DrillPointAngle = 118
  HoleCutCountersinkAngle = 90
  HoleCutCustomValues = false
  HoleCutDepth = 0
  HoleCutDiameter = 0
  HoleCutType = 0
  ModelThread = false
  Profile = -> Sketch018
  Refine = true
  Suppressed = false
  Tapered = false
  TaperedAngle = 90
  ThreadClass = 0
  ThreadDepth = 2.5
  ThreadDepthType = 0
  ThreadDiameter = 2.5
  ThreadDirection = 0
  ThreadFit = 0
  ThreadSize = 8
  ThreadType = 1
  Threaded = false
  UseCustomThreadClearance = false
FEATURE [PartDesign::Body] Body002  label="horn_holder"
  AllowCompound = true
  Group = -> [Sketch012,Pad003,Sketch013,Hole005,Sketch014,Pad004,Fillet,Sketch015,Pad005,Sketch016,Hole006,Sketch017,Hole002,Sketch018,Hole007]
  Origin = -> Origin013
  Tip = -> Hole007
FEATURE [App::Point] Origin017  label="Origin019"
  Role = Origin
FEATURE [App::Link] base  label="base001"
  LinkedObject = -> Body
FEATURE [App::FeaturePython] GroundedJoint  label="GroundedJoint001"  # Assembly grounded joint (typed FeaturePython)
  ObjectToGround = -> base
FEATURE [App::Link] mx_28_holder  label="mx_28_holder001"
  LinkPlacement = pos=(125,1.04e-14,44.6) rot=(-0.57735,0.57735,0.57735;4.18879rad)
  LinkedObject = -> Body001
  Placement = pos=(125,1.04e-14,44.6) rot=(-0.57735,0.57735,0.57735;4.18879rad)
FEATURE [App::FeaturePython] Joint  label="Fixed012"  # Assembly joint (typed FeaturePython)
  Angle = 0
  AngleMax = 0
  AngleMin = 0
  Detach1 = false
  Detach2 = false
  Distance = 0
  Distance2 = 0
  EnableAngleMax = false
  EnableAngleMin = false
  EnableLengthMax = false
  EnableLengthMin = false
  JointType = 0 (Fixed)
  LengthMax = 0
  LengthMin = 0
  Offset2 = pos=(0,0,0) rot=(0,0,-1;1.5708rad)
  Placement1 = pos=(119,0,3) rot=(0,0,1;0rad)
  Placement2 = pos=(0,-41.6,6) rot=(0.57735,0.57735,-0.57735;2.0944rad)
  Reference1 = -> base [Edge116,Edge116]
  Reference2 = -> mx_28_holder [Edge32,Edge32]
  Suppressed = false
FEATURE [App::Link] mx28  label="mx001"
  LinkPlacement = pos=(126,1.82e-14,44.6) rot=(0.57735,-0.57735,-0.57735;2.0944rad)
  LinkedObject = -> Unnamed
  Placement = pos=(126,1.82e-14,44.6) rot=(0.57735,-0.57735,-0.57735;2.0944rad)
FEATURE [App::FeaturePython] Joint001  label="Fixed013"  # Assembly joint (typed FeaturePython)
  Angle = 0
  AngleMax = 0
  AngleMin = 0
  Detach1 = false
  Detach2 = false
  Distance = 0
  Distance2 = 0
  EnableAngleMax = false
  EnableAngleMin = false
  EnableLengthMax = false
  EnableLengthMin = false
  JointType = 0 (Fixed)
  LengthMax = 0
  LengthMin = 0
  Placement1 = pos=(15,-29.5,15) rot=(0,0,1;0rad)
  Placement2 = pos=(15,-29.5,15) rot=(1,0,0;3.14159rad)
  Reference1 = -> mx_28_holder [Edge46,Edge46]
  Reference2 = -> mx28 [Part__Feature.Edge701,Part__Feature.Edge701]
  Suppressed = false
FEATURE [App::Link] horn_holder  label="horn_holder001"
  LinkPlacement = pos=(-105.4,-1.76093e-05,3) rot=(0,0,1;0rad)
  LinkedObject = -> Body002
  Placement = pos=(-105.4,-1.76093e-05,3) rot=(0,0,1;0rad)
FEATURE [App::FeaturePython] Joint002  label="Fixed014"  # Assembly joint (typed FeaturePython)
  Angle = 0
  AngleMax = 0
  AngleMin = 0
  Detach1 = false
  Detach2 = false
  Distance = 0
  Distance2 = 0
  EnableAngleMax = false
  EnableAngleMin = false
  EnableLengthMax = false
  EnableLengthMin = false
  JointType = 0 (Fixed)
  LengthMax = 0
  LengthMin = 0
  Placement1 = pos=(-97.9,-7.50002,3) rot=(0,0,1;0rad)
  Placement2 = pos=(7.5,-7.5,0) rot=(0,0,1;0rad)
  Reference1 = -> base [Edge79,Edge79]
  Reference2 = -> horn_holder [Edge36,Edge36]
  Suppressed = false
FEATURE [App::Link] HN07_I_002
  LinkPlacement = pos=(-102.9,-1.76093e-05,45) rot=(0.618936,-0.618936,-0.483566;4.04242rad)
  LinkedObject = -> HN07_I_001
  Placement = pos=(-102.9,-1.76093e-05,45) rot=(0.618936,-0.618936,-0.483566;4.04242rad)
FEATURE [App::FeaturePython] Joint003  label="Fixed015"  # Assembly joint (typed FeaturePython)
  Angle = 0
  AngleMax = 0
  AngleMin = 0
  Detach1 = false
  Detach2 = false
  Distance = 0
  Distance2 = 0
  EnableAngleMax = false
  EnableAngleMin = false
  EnableLengthMax = false
  EnableLengthMin = false
  JointType = 0 (Fixed)
  LengthMax = 0
  LengthMin = 0
  Offset2 = pos=(0,0,0) rot=(0,0,-1;0.244346rad)
  Placement1 = pos=(2.5,0,42) rot=(0,1,0;1.5708rad)
  Placement2 = pos=(0,0,0) rot=(-0.985257,-0.120974,-0.120974;1.58565rad)
  Reference1 = -> horn_holder [Edge48,Edge48]
  Reference2 = -> HN07_I_002 [Part__Feature005.Edge44,Part__Feature005.Edge44]
  Suppressed = false
FEATURE [App::Link] horn_holder001  label="horn_holder002"
  LinkPlacement = pos=(-97.4,0.0241704,86.2) rot=(1,0,0;3.14101rad)
  LinkedObject = -> Body002
  Placement = pos=(-97.4,0.0241704,86.2) rot=(1,0,0;3.14101rad)
FEATURE [App::FeaturePython] Joint004  label="Revolute018"  # Assembly joint (typed FeaturePython)
  Angle = 0
  AngleMax = 0
  AngleMin = 0
  Detach1 = false
  Detach2 = false
  Distance = 0
  Distance2 = 0
  EnableAngleMax = false
  EnableAngleMin = false
  EnableLengthMax = false
  EnableLengthMin = false
  JointType = 1 (Revolute)
  LengthMax = 0
  LengthMin = 0
  Offset2 = pos=(0,0,-8) rot=(0,0,1;0rad)
  Placement1 = pos=(-2.5,0,41.6) rot=(0,-1,0;1.5708rad)
  Placement2 = pos=(5.5,0,41.6) rot=(0,-1,0;1.5708rad)
  Reference1 = -> horn_holder001 [Edge58,Edge58]
  Reference2 = -> horn_holder [Edge58,Edge58]
  Suppressed = false
FEATURE [App::Link] horn_holder002  label="horn_holder003"
  LinkPlacement = pos=(101.55,-0.037515,86.6) rot=(1,0,0;3.14249rad)
  LinkedObject = -> Body002
  Placement = pos=(101.55,-0.037515,86.6) rot=(1,0,0;3.14249rad)
FEATURE [App::FeaturePython] Joint005  label="Revolute019"  # Assembly joint (typed FeaturePython)
  Angle = 0
  AngleMax = 0
  AngleMin = 0
  Detach1 = false
  Detach2 = false
  Distance = 0
  Distance2 = 0
  EnableAngleMax = false
  EnableAngleMin = false
  EnableLengthMax = false
  EnableLengthMin = false
  JointType = 1 (Revolute)
  LengthMax = 0
  LengthMin = 0
  Offset2 = pos=(0,0,-2) rot=(0,0,1;0rad)
  Placement1 = pos=(2.5,0,42) rot=(0,1,0;1.5708rad)
  Placement2 = pos=(0,2.65,0) rot=(0,0.707107,0.707107;3.14159rad)
  Reference1 = -> horn_holder002 [Edge48,Edge48]
  Reference2 = -> mx28 [HN07_N_02.Part__Feature003.Edge261,HN07_N_02.Part__Feature003.Edge261]
  Suppressed = false
FEATURE [App::Link] Body003  label="Body"
  LinkPlacement = pos=(2.25,-0.037515,86.6) rot=(1,0,0;0.000893rad)
  LinkedObject = -> <external Unnamed1.FCStd>#Body
  Placement = pos=(2.25,-0.037515,86.6) rot=(1,0,0;0.000893rad)
FEATURE [App::FeaturePython] Joint006  label="Fixed016"  # Assembly joint (typed FeaturePython)
  Angle = 0
  AngleMax = 0
  AngleMin = 0
  Detach1 = false
  Detach2 = false
  Distance = 0
  Distance2 = 0
  EnableAngleMax = false
  EnableAngleMin = false
  EnableLengthMax = false
  EnableLengthMin = false
  JointType = 0 (Fixed)
  LengthMax = 0
  LengthMin = 0
  Placement1 = pos=(7.5,7.5,0) rot=(0,0,1;0rad)
  Placement2 = pos=(106.8,-7.5,0) rot=(0,0,1;0rad)
  Reference1 = -> horn_holder002 [Edge40,Edge40]
  Reference2 = -> Body003 [Edge15,Edge15]
  Suppressed = false
FEATURE [Assembly::JointGroup] Joints
  Group = -> [GroundedJoint,Joint,Joint001,Joint002,Joint003,Joint004,Joint005,Joint006]
FEATURE [Assembly::AssemblyObject] Assembly
  Group = -> [Joints,base,GroundedJoint,mx_28_holder,Joint,mx28,Joint001,horn_holder,Joint002,HN07_I_002,Joint003,horn_holder001,Joint004,horn_holder002,Joint005,Body003,Joint006]
  Origin = -> Origin016
  Type = Assembly
FEATURE [TechDraw::DrawSVGTemplate] Template
  Height = 210
  Orientation = 1
  Template = <path>
  Width = 297
FEATURE [TechDraw::DrawProjGroupItem] View
  CoarseView = false
  Direction = (0,0,1)
  Focus = 100
  HardHidden = false
  IsoCount = 0
  IsoHidden = false
  IsoVisible = false
  LockPosition = false
  Perspective = false
  Rotation = 0
  RotationVector = (1,0,0)
  ScaleType = 0
  ScrubCount = 1
  SeamHidden = false
  SeamVisible = false
  SmoothHidden = false
  SmoothVisible = true
  Source = -> [Body]
  Type = 0
  X = 148.5
  XDirection = (1,0,0)
  Y = 105
FEATURE [TechDraw::DrawViewDimension] Dimension
  AngleOverride = false
  Arbitrary = false
  ArbitraryTolerances = false
  BoxCorners = (2) [(-200,-75,0),(200,75,0)]
  EqualTolerance = true
  ExtensionAngle = 0
  FormatSpec = %.2w
  FormatSpecOverTolerance = %+.2w
  FormatSpecUnderTolerance = %+.2w
  Inverted = false
  LineAngle = 0
  LockPosition = false
  MeasureType = 1
  OverTolerance = 0
  References2D = -> [View]
  Rotation = 0
  ScaleType = 0
  ShowUnits = false
  TheoreticalExact = false
  Type = 1
  UnderTolerance = 0
  UseActualArea = true
  X = -28.9999
  Y = 140.948
FEATURE [TechDraw::DrawViewDimension] Dimension001
  AngleOverride = false
  Arbitrary = false
  ArbitraryTolerances = false
  BoxCorners = (2) [(-200,-75,0),(200,75,0)]
  EqualTolerance = true
  ExtensionAngle = 0
  FormatSpec = %.2w
  FormatSpecOverTolerance = %+.2w
  FormatSpecUnderTolerance = %+.2w
  Inverted = false
  LineAngle = 0
  LockPosition = false
  MeasureType = 1
  OverTolerance = 0
  References2D = -> [View]
  Rotation = 0
  ScaleType = 0
  ShowUnits = false
  TheoreticalExact = false
  Type = 2
  UnderTolerance = 0
  UseActualArea = true
  X = -255.352
  Y = -3.69658
FEATURE [TechDraw::DrawPage] Page
  KeepUpdated = true
  NextBalloonIndex = 1
  ProjectionType = 0
  Template = -> Template
  Views = -> [View,Dimension,Dimension001]
note: 1 file-system path scrubbed to <path> (originals preserved in the JSON sidecar)

RESOLVED EXTERNAL PARTS (link-assembly join: the EXTERNAL_REF files above that resolve inside this repo's crawl, each included once):
---- part Unnamed1.FCStd = doc fcstd_f545d43962c9 ----
FCSTD DOCUMENT  (FreeCAD 1.1R20260414 (Git shallow))
Label: Unnamed1
License: All rights reserved
LicenseURL: https://en.wikipedia.org/wiki/All_rights_reserved
objects: Sketcher::SketchObject×25, PartDesign::Pad×13, PartDesign::Hole×11, PartDesign::Fillet×10, App::Point×5, PartDesign::Body×5, PartDesign::Mirrored×2, TechDraw::DrawViewDimension×2, PartDesign::ShapeBinder×2, PartDesign::Pocket×1, TechDraw::DrawSVGTemplate×1, TechDraw::DrawProjGroupItem×1, TechDraw::DrawPage×1
note: 168 computed .brp shape members not serialized (recipe doc carries the construction recipe); baked Part::Feature solids carry a one-line shape summary decoded from their .brp

FEATURE [App::Point] Origin001
  Role = Origin
FEATURE [Sketcher::SketchObject] Sketch
  ArcFitTolerance = 1e-06
  AttachmentSupport = -> [Origin]
  ExternalTypes = [0]
  FullyConstrained = true
  MakeInternals = false
  MapMode = 5
  _ExternalGeoVersion = 1
  sketch-geometry (5):
    g0: LineSegment StartX=-114.3 StartY=-90 StartZ=0 EndX=114.3 EndY=-90 EndZ=0
    g1: LineSegment StartX=114.3 StartY=-90 StartZ=0 EndX=114.3 EndY=90 EndZ=0
    g2: LineSegment StartX=114.3 StartY=90 StartZ=0 EndX=-114.3 EndY=90 EndZ=0
    g3: LineSegment StartX=-114.3 StartY=90 StartZ=0 EndX=-114.3 EndY=-90 EndZ=0
    g4: GeomPoint [constr] X=0 Y=0 Z=0
  constraints (12):
    c: Coincident(g0,g1)
    c: Coincident(g1,g2)
    c: Coincident(g2,g3)
    c: Coincident(g3,g0)
    c: Horizontal(g0)
    c: Horizontal(g2)
    c: Vertical(g1)
    c: Vertical(g3)
    c: Symmetric(g2,g0,g4)
    c: Distance(g1,g3) = 228.6
    c: Distance(g0,g2) = 180
    c: Coincident(g4,g-1)
FEATURE [PartDesign::Pad] Pad
  Direction = (0,0,1)
  Length = 5
  Length2 = 10
  Profile = -> Sketch
  ReferenceAxis = -> Sketch [N_Axis]
  Refine = true
  SideType = 0
  Suppressed = false
  Type = 0
  Type2 = 0
FEATURE [Sketcher::SketchObject] Sketch001
  ArcFitTolerance = 1e-06
  AttachmentSupport = -> [Pad]
  ExternalTypes = [0]
  FullyConstrained = true
  MakeInternals = false
  MapMode = 5
  Placement = pos=(0,0,5) rot=(0,0,1;0rad)
  _ExternalGeoVersion = 1
  sketch-geometry (8):
    g0: Circle CenterX=106.8 CenterY=7.5 CenterZ=0 NormalX=0 NormalY=0 NormalZ=1 AngleXU=0 Radius=1.1
    g1: Circle CenterX=106.8 CenterY=-7.5 CenterZ=0 NormalX=0 NormalY=0 NormalZ=1 AngleXU=0 Radius=1.1
    g2: Circle CenterX=91.8 CenterY=7.5 CenterZ=0 NormalX=0 NormalY=0 NormalZ=1 AngleXU=0 Radius=1.1
    g3: Circle CenterX=91.8 CenterY=-7.5 CenterZ=0 NormalX=0 NormalY=0 NormalZ=1 AngleXU=0 Radius=1.1
    g4: Circle CenterX=71.8 CenterY=7.5 CenterZ=0 NormalX=0 NormalY=0 NormalZ=1 AngleXU=0 Radius=1.1
    g5: Circle CenterX=71.8 CenterY=-7.5 CenterZ=0 NormalX=0 NormalY=0 NormalZ=1 AngleXU=0 Radius=1.1
    g6: Circle CenterX=56.8 CenterY=7.5 CenterZ=0 NormalX=0 NormalY=0 NormalZ=1 AngleXU=0 Radius=1.1
    g7: Circle CenterX=56.8 CenterY=-7.5 CenterZ=0 NormalX=0 NormalY=0 NormalZ=1 AngleXU=0 Radius=1.1
  constraints (24):
    c: Diameter(g1) = 2.2
    c: Equal(g0,g1)
    c: DistanceX(g-1,g0) = 106.8
    c: DistanceX(g-1,g1) = 106.8
    c: Equal(g0,g2)
    c: Equal(g2,g3)
    c: DistanceX(g-1,g2) = 91.8
    c: DistanceX(g-1,g3) = 91.8
    c: Distance(g2,g-1) = 7.5
    c: Distance(g3,g-1) = 7.5
    c: Distance(g0,g-1) = 7.5
    c: Distance(g1,g-1) = 7.5
    c: Equal(g2,g4)
    c: Equal(g3,g5)
    c: DistanceX(g4,g2) = 20
    c: DistanceX(g5,g3) = 20
    c: Distance(g4,g-1) = 7.5
    c: Distance(g5,g-1) = 7.5
    c: Equal(g5,g7)
    c: Equal(g7,g6)
    c: DistanceX(g6,g4) = 15
    c: DistanceX(g7,g5) = 15
    c: Distance(g7,g-1) = 7.5
    c: Distance(g6,g-1) = 7.5
FEATURE [PartDesign::Hole] Hole
  BaseFeature = -> Pad
  BaseProfileType = 7
  CustomThreadClearance = 0
  Depth = 5
  DepthType = 0
  Diameter = 2.9
  DrillForDepth = false
  DrillPoint = 1
  DrillPointAngle = 118
  HoleCutCountersinkAngle = 90
  HoleCutCustomValues = false
  HoleCutDepth = 0
  HoleCutDiameter = 0
  HoleCutType = 0
  ModelThread = false
  Profile = -> Sketch001
  Refine = true
  Suppressed = false
  Tapered = false
  TaperedAngle = 90
  ThreadClass = 0
  ThreadDepth = 5
  ThreadDepthType = 0
  ThreadDiameter = 2.5
  ThreadDirection = 0
  ThreadFit = 0
  ThreadSize = 8
  ThreadType = 1
  Threaded = false
  UseCustomThreadClearance = false
FEATURE [PartDesign::Mirrored] Mirrored
  BaseFeature = -> Hole
  MirrorPlane = -> Sketch001 [V_Axis]
  Originals = -> [Hole]
  Refine = true
  Suppressed = false
  TransformMode = 0
FEATURE [App::Point] Origin012  label="Origin014"
  Role = Origin
FEATURE [Sketcher::SketchObject] Sketch012
  ArcFitTolerance = 1e-06
  AttachmentSupport = -> [Origin013]
  ExternalTypes = [0]
  FullyConstrained = true
  MakeInternals = false
  MapMode = 5
  _ExternalGeoVersion = 1
  sketch-geometry (5):
    g0: LineSegment StartX=-12 StartY=-12 StartZ=0 EndX=12 EndY=-12 EndZ=0
    g1: LineSegment StartX=12 StartY=-12 StartZ=0 EndX=12 EndY=12 EndZ=0
    g2: LineSegment StartX=12 StartY=12 StartZ=0 EndX=-12 EndY=12 EndZ=0
    g3: LineSegment StartX=-12 StartY=12 StartZ=0 EndX=-12 EndY=-12 EndZ=0
    g4: GeomPoint [constr] X=0 Y=0 Z=0
  constraints (12):
    c: Coincident(g0,g1)
    c: Coincident(g1,g2)
    c: Coincident(g2,g3)
    c: Coincident(g3,g0)
    c: Horizontal(g0)
    c: Horizontal(g2)
    c: Vertical(g1)
    c: Vertical(g3)
    c: Symmetric(g2,g0,g4)
    c: Distance(g1,g3) = 24
    c: Distance(g0,g2) = 24
    c: Coincident(g4,g-1)
FEATURE [PartDesign::Pad] Pad003
  Direction = (0,0,1)
  Length = 5
  Length2 = 10
  Profile = -> Sketch012
  ReferenceAxis = -> Sketch012 [N_Axis]
  Refine = true
  SideType = 0
  Suppressed = false
  Type = 0
  Type2 = 0
FEATURE [Sketcher::SketchObject] Sketch013
  ArcFitTolerance = 1e-06
  AttachmentSupport = -> [Pad003]
  ExternalTypes = [0]
  FullyConstrained = true
  MakeInternals = false
  MapMode = 5
  Placement = pos=(0,0,5) rot=(0,0,1;0rad)
  _ExternalGeoVersion = 1
  sketch-geometry (5):
    g0: GeomPoint [constr] X=0 Y=0 Z=0
    g1: Circle CenterX=7.5 CenterY=7.5 CenterZ=0 NormalX=0 NormalY=0 NormalZ=1 AngleXU=0 Radius=1.1
    g2: Circle CenterX=-7.5 CenterY=7.5 CenterZ=0 NormalX=0 NormalY=0 NormalZ=1 AngleXU=0 Radius=1.1
    g3: Circle CenterX=-7.5 CenterY=-7.5 CenterZ=0 NormalX=0 NormalY=0 NormalZ=1 AngleXU=0 Radius=1.1
    g4: Circle CenterX=7.5 CenterY=-7.5 CenterZ=0 NormalX=0 NormalY=0 NormalZ=1 AngleXU=0 Radius=1.1
  constraints (12):
    c: Symmetric(g1,g3,g0)
    c: Distance(g4,g3) = 15
    c: Distance(g3,g2) = 15
    c: Coincident(g0,g-1)
    c: Diameter(g1) = 2.2
    c: Equal(g1,g2)
    c: Equal(g2,g3)
    c: Equal(g3,g4)
    c: DistanceX(g2,g1) = 15
    c: DistanceY(g4,g1) = 15
    c: Distance(g4,g-2) = 7.5
    c: Distance(g2,g-1) = 7.5
FEATURE [PartDesign::Hole] Hole005
  BaseFeature = -> Pad003
  BaseProfileType = 7
  CustomThreadClearance = 0
  Depth = 5
  DepthType = 0
  Diameter = 2.9
  DrillForDepth = false
  DrillPoint = 1
  DrillPointAngle = 118
  HoleCutCountersinkAngle = 90
  HoleCutCustomValues = false
  HoleCutDepth = 0
  HoleCutDiameter = 0
  HoleCutType = 0
  ModelThread = false
  Profile = -> Sketch013
  Refine = true
  Suppressed = false
  Tapered = false
  TaperedAngle = 90
  ThreadClass = 0
  ThreadDepth = 5
  ThreadDepthType = 0
  ThreadDiameter = 2.5
  ThreadDirection = 0
  ThreadFit = 0
  ThreadSize = 8
  ThreadType = 1
  Threaded = false
  UseCustomThreadClearance = false
FEATURE [Sketcher::SketchObject] Sketch014
  ArcFitTolerance = 1e-06
  AttachmentSupport = -> [Hole005]
  ExternalTypes = [0]
  FullyConstrained = true
  MakeInternals = false
  MapMode = 5
  Placement = pos=(0,0,5) rot=(0,0,1;0rad)
  _ExternalGeoVersion = 1
  sketch-geometry (5):
    g0: LineSegment StartX=-2.5 StartY=-11 StartZ=0 EndX=2.5 EndY=-11 EndZ=0
    g1: LineSegment StartX=2.5 StartY=-11 StartZ=0 EndX=2.5 EndY=11 EndZ=0
    g2: LineSegment StartX=2.5 StartY=11 StartZ=0 EndX=-2.5 EndY=11 EndZ=0
    g3: LineSegment StartX=-2.5 StartY=11 StartZ=0 EndX=-2.5 EndY=-11 EndZ=0
    g4: GeomPoint [constr] X=0 Y=0 Z=0
  constraints (12):
    c: Coincident(g0,g1)
    c: Coincident(g1,g2)
    c: Coincident(g2,g3)
    c: Coincident(g3,g0)
    c: Horizontal(g0)
    c: Horizontal(g2)
    c: Vertical(g1)
    c: Vertical(g3)
    c: Symmetric(g2,g0,g4)
    c: Distance(g1,g3) = 5
    c: Distance(g0,g2) = 22
    c: Coincident(g4,g-1)
FEATURE [PartDesign::Pad] Pad004
  BaseFeature = -> Hole005
  Direction = (0,0,1)
  Length = 37
  Length2 = 10
  Profile = -> Sketch014
  ReferenceAxis = -> Sketch014 [N_Axis]
  Refine = true
  SideType = 0
  Suppressed = false
  Type = 0
  Type2 = 0
FEATURE [PartDesign::Fillet] Fillet
  Base = -> Pad004 [Edge23,Edge21]
  BaseFeature = -> Pad004
  Radius = 3
  Refine = true
  SupportTransform = false
  Suppressed = false
  UseAllEdges = false
FEATURE [Sketcher::SketchObject] Sketch015
  ArcFitTolerance = 1e-06
  AttachmentSupport = -> [Fillet]
  ExternalTypes = [0,0]
  FullyConstrained = true
  MakeInternals = false
  MapMode = 5
  Placement = pos=(-2.5,0,0) rot=(0.57735,-0.57735,-0.57735;2.0944rad)
  _ExternalGeoVersion = 1
  sketch-geometry (2):
    g0: ArcOfCircle CenterX=6.6e-13 CenterY=42 CenterZ=0 NormalX=0 NormalY=0 NormalZ=1 AngleXU=0 Radius=11 StartAngle=0 EndAngle=3.14159
    g1: LineSegment StartX=-11 StartY=42 StartZ=0 EndX=11 EndY=42 EndZ=0
  constraints (7):
    c: Coincident(g1,g0)
    c: Coincident(g1,g0)
    c: DistanceY(g-1,g0) = 42
    c: DistanceY(g-1,g0) = 42
    c: Distance(g0,g-2) = 11
    c: Distance(g0,g-2) = 11
    c: Distance(g0,g-1) = 31
FEATURE [PartDesign::Pad] Pad005
  BaseFeature = -> Fillet
  Direction = (-1,0,0)
  Length = 5
  Length2 = 10
  Profile = -> Sketch015
  ReferenceAxis = -> Sketch015 [N_Axis]
  Refine = true
  Reversed = true
  SideType = 0
  Suppressed = false
  Type = 0
  Type2 = 0
FEATURE [Sketcher::SketchObject] Sketch016
  ArcFitTolerance = 1e-06
  AttachmentSupport = -> [Pad005]
  ExternalTypes = [0]
  FullyConstrained = true
  MakeInternals = false
  MapMode = 5
  Placement = pos=(2.5,0,0) rot=(0.57735,0.57735,0.57735;2.0944rad)
  _ExternalGeoVersion = 1
  sketch-geometry (8):
    g0: Circle CenterX=-6.87 CenterY=37.91 CenterZ=0 NormalX=0 NormalY=0 NormalZ=1 AngleXU=0 Radius=0.75
    g1: Circle CenterX=-7.75 CenterY=43.96 CenterZ=0 NormalX=0 NormalY=0 NormalZ=1 AngleXU=0 Radius=0.75
    g2: Circle CenterX=-4.1 CenterY=48.87 CenterZ=0 NormalX=0 NormalY=0 NormalZ=1 AngleXU=0 Radius=0.75
    g3: Circle CenterX=1.96 CenterY=49.75 CenterZ=0 NormalX=0 NormalY=0 NormalZ=1 AngleXU=0 Radius=0.75
    g4: Circle CenterX=6.87 CenterY=46.09 CenterZ=0 NormalX=0 NormalY=0 NormalZ=1 AngleXU=0 Radius=0.75
    g5: Circle CenterX=7.75 CenterY=40.04 CenterZ=0 NormalX=0 NormalY=0 NormalZ=1 AngleXU=0 Radius=0.75
    g6: Circle CenterX=4.1 CenterY=35.13 CenterZ=0 NormalX=0 NormalY=0 NormalZ=1 AngleXU=0 Radius=0.75
    g7: Circle CenterX=-1.97 CenterY=34.24 CenterZ=0 NormalX=0 NormalY=0 NormalZ=1 AngleXU=0 Radius=0.75
  constraints (24):
    c: Diameter(g0) = 1.5
    c: Distance(g0,g-2) = 6.87
    c: Distance(g0,g-1) = 37.91
    c: Equal(g0,g1)
    c: Equal(g1,g2)
    c: Equal(g2,g3)
    c: Equal(g3,g4)
    c: Equal(g4,g5)
    c: Equal(g5,g6)
    c: Equal(g6,g7)
    c: Distance(g1,g-2) = 7.75
    c: Distance(g2,g-2) = 4.1
    c: Distance(g3,g-2) = 1.96
    c: Distance(g4,g-2) = 6.87
    c: Distance(g5,g-2) = 7.75
    c: Distance(g6,g-2) = 4.1
    c: Distance(g7,g-2) = 1.97
    c: Distance(g7,g-1) = 34.24
    c: DistanceY(g-1,g1) = 43.96
    c: DistanceY(g-1,g2) = 48.87
    c: DistanceY(g-1,g3) = 49.75
    c: DistanceY(g-1,g4) = 46.09
    c: DistanceY(g-1,g5) = 40.04
    c: DistanceY(g-1,g6) = 35.13
FEATURE [PartDesign::Hole] Hole006
  BaseFeature = -> Pad005
  BaseProfileType = 7
  CustomThreadClearance = 0
  Depth = 5
  DepthType = 0
  Diameter = 2.552
  DrillForDepth = false
  DrillPoint = 1
  DrillPointAngle = 118
  HoleCutCountersinkAngle = 90
  HoleCutCustomValues = false
  HoleCutDepth = 0
  HoleCutDiameter = 0
  HoleCutType = 0
  ModelThread = false
  Profile = -> Sketch016
  Refine = true
  Suppressed = false
  Tapered = false
  TaperedAngle = 90
  ThreadClass = 0
  ThreadDepth = 5
  ThreadDepthType = 0
  ThreadDiameter = 2.2
  ThreadDirection = 0
  ThreadFit = 2
  ThreadSize = 7
  ThreadType = 1
  Threaded = false
  UseCustomThreadClearance = false
FEATURE [Sketcher::SketchObject] Sketch017
  ArcFitTolerance = 1e-06
  AttachmentSupport = -> [Hole006]
  ExternalTypes = [0,0]
  FullyConstrained = true
  MakeInternals = false
  MapMode = 5
  Placement = pos=(2.5,0,0) rot=(0.57735,0.57735,0.57735;2.0944rad)
  _ExternalGeoVersion = 1
  sketch-geometry (1):
    g0: Circle CenterX=0 CenterY=42 CenterZ=0 NormalX=0 NormalY=0 NormalZ=1 AngleXU=0 Radius=5.5
  constraints (3):
    c: Diameter(g0) = 11
    c: PointOnObject(g0,g-2)
    c: DistanceY(g-1,g0) = 42
FEATURE [PartDesign::Hole] Hole002
  BaseFeature = -> Hole006
  BaseProfileType = 7
  CustomThreadClearance = 0
  Depth = 2.5
  DepthType = 0
  Diameter = 9
  DrillForDepth = false
  DrillPoint = 1
  DrillPointAngle = 118
  HoleCutCountersinkAngle = 90
  HoleCutCustomValues = false
  HoleCutDepth = 0
  HoleCutDiameter = 0
  HoleCutType = 0
  ModelThread = false
  Profile = -> Sketch017
  Refine = true
  Suppressed = false
  Tapered = false
  TaperedAngle = 90
  ThreadClass = 0
  ThreadDepth = 2.5
  ThreadDepthType = 0
  ThreadDiameter = 8
  ThreadDirection = 0
  ThreadFit = 0
  ThreadSize = 16
  ThreadType = 1
  Threaded = false
  UseCustomThreadClearance = false
FEATURE [Sketcher::SketchObject] Sketch018
  ArcFitTolerance = 1e-06
  AttachmentSupport = -> [Hole002]
  ExternalTypes = [0]
  FullyConstrained = true
  MakeInternals = false
  MapMode = 5
  Placement = pos=(-2.5,0,0) rot=(0.57735,-0.57735,-0.57735;2.0944rad)
  _ExternalGeoVersion = 1
  sketch-geometry (1):
    g0: Circle CenterX=0 CenterY=41.6 CenterZ=0 NormalX=0 NormalY=0 NormalZ=1 AngleXU=0 Radius=1.1
  constraints (3):
    c: Diameter(g0) = 2.2
    c: PointOnObject(g0,g-2)
    c: DistanceY(g-1,g0) = 41.6
FEATURE [PartDesign::Hole] Hole007
  BaseFeature = -> Hole002
  BaseProfileType = 7
  CustomThreadClearance = 0
  Depth = 2.5
  DepthType = 0
  Diameter = 2.9
  DrillForDepth = false
  DrillPoint = 1
  DrillPointAngle = 118
  HoleCutCountersinkAngle = 90
  HoleCutCustomValues = false
  HoleCutDepth = 0
  HoleCutDiameter = 0
  HoleCutType = 0
  ModelThread = false
  Profile = -> Sketch018
  Refine = true
  Suppressed = false
  Tapered = false
  TaperedAngle = 90
  ThreadClass = 0
  ThreadDepth = 2.5
  ThreadDepthType = 0
  ThreadDiameter = 2.5
  ThreadDirection = 0
  ThreadFit = 0
  ThreadSize = 8
  ThreadType = 1
  Threaded = false
  UseCustomThreadClearance = false
FEATURE [PartDesign::Body] Body002  label="horn_holder"
  AllowCompound = true
  Group = -> [Sketch012,Pad003,Sketch013,Hole005,Sketch014,Pad004,Fillet,Sketch015,Pad005,Sketch016,Hole006,Sketch017,Hole002,Sketch018,Hole007]
  Origin = -> Origin013
  Tip = -> Hole007
FEATURE [App::Point] Origin014  label="Origin016"
  Role = Origin
FEATURE [Sketcher::SketchObject] Sketch019
  ArcFitTolerance = 1e-06
  AttachmentSupport = -> [Origin015]
  ExternalTypes = [0]
  FullyConstrained = true
  MakeInternals = false
  MapMode = 5
  _ExternalGeoVersion = 1
  sketch-geometry (5):
    g0: LineSegment StartX=-12 StartY=-12 StartZ=0 EndX=12 EndY=-12 EndZ=0
    g1: LineSegment StartX=12 StartY=-12 StartZ=0 EndX=12 EndY=12 EndZ=0
    g2: LineSegment StartX=12 StartY=12 StartZ=0 EndX=-12 EndY=12 EndZ=0
    g3: LineSegment StartX=-12 StartY=12 StartZ=0 EndX=-12 EndY=-12 EndZ=0
    g4: GeomPoint [constr] X=0 Y=0 Z=0
  constraints (12):
    c: Coincident(g0,g1)
    c: Coincident(g1,g2)
    c: Coincident(g2,g3)
    c: Coincident(g3,g0)
    c: Horizontal(g0)
    c: Horizontal(g2)
    c: Vertical(g1)
    c: Vertical(g3)
    c: Symmetric(g2,g0,g4)
    c: Distance(g1,g3) = 24
    c: Distance(g0,g2) = 24
    c: Coincident(g4,g-1)
FEATURE [PartDesign::Pad] Pad006
  Direction = (0,0,1)
  Length = 5
  Length2 = 10
  Profile = -> Sketch019
  ReferenceAxis = -> Sketch019 [N_Axis]
  Refine = true
  SideType = 0
  Suppressed = false
  Type = 0
  Type2 = 0
FEATURE [Sketcher::SketchObject] Sketch020
  ArcFitTolerance = 1e-06
  AttachmentSupport = -> [Pad006]
  ExternalTypes = [0]
  FullyConstrained = true
  MakeInternals = false
  MapMode = 5
  Placement = pos=(0,0,5) rot=(0,0,1;0rad)
  _ExternalGeoVersion = 1
  sketch-geometry (5):
    g0: GeomPoint [constr] X=0 Y=0 Z=0
    g1: Circle CenterX=7.5 CenterY=7.5 CenterZ=0 NormalX=0 NormalY=0 NormalZ=1 AngleXU=0 Radius=1.1
    g2: Circle CenterX=-7.5 CenterY=7.5 CenterZ=0 NormalX=0 NormalY=0 NormalZ=1 AngleXU=0 Radius=1.1
    g3: Circle CenterX=-7.5 CenterY=-7.5 CenterZ=0 NormalX=0 NormalY=0 NormalZ=1 AngleXU=0 Radius=1.1
    g4: Circle CenterX=7.5 CenterY=-7.5 CenterZ=0 NormalX=0 NormalY=0 NormalZ=1 AngleXU=0 Radius=1.1
  constraints (12):
    c: Symmetric(g1,g3,g0)
    c: Distance(g4,g3) = 15
    c: Distance(g3,g2) = 15
    c: Coincident(g0,g-1)
    c: Diameter(g1) = 2.2
    c: Equal(g1,g2)
    c: Equal(g2,g3)
    c: Equal(g3,g4)
    c: DistanceX(g2,g1) = 15
    c: DistanceY(g4,g1) = 15
    c: Distance(g4,g-2) = 7.5
    c: Distance(g2,g-1) = 7.5
FEATURE [PartDesign::Hole] Hole009
  BaseFeature = -> Pad006
  BaseProfileType = 7
  CustomThreadClearance = 0
  Depth = 5
  DepthType = 0
  Diameter = 2.9
  DrillForDepth = false
  DrillPoint = 1
  DrillPointAngle = 118
  HoleCutCountersinkAngle = 90
  HoleCutCustomValues = false
  HoleCutDepth = 0
  HoleCutDiameter = 0
  HoleCutType = 0
  ModelThread = false
  Profile = -> Sketch020
  Refine = true
  Suppressed = false
  Tapered = false
  TaperedAngle = 90
  ThreadClass = 0
  ThreadDepth = 5
  ThreadDepthType = 0
  ThreadDiameter = 2.5
  ThreadDirection = 0
  ThreadFit = 0
  ThreadSize = 8
  ThreadType = 1
  Threaded = false
  UseCustomThreadClearance = false
FEATURE [Sketcher::SketchObject] Sketch021
  ArcFitTolerance = 1e-06
  AttachmentSupport = -> [Hole009]
  ExternalTypes = [0]
  FullyConstrained = true
  MakeInternals = false
  MapMode = 5
  Placement = pos=(0,0,5) rot=(0,0,1;0rad)
  _ExternalGeoVersion = 1
  sketch-geometry (5):
    g0: LineSegment StartX=-2.5 StartY=-11 StartZ=0 EndX=2.5 EndY=-11 EndZ=0
    g1: LineSegment StartX=2.5 StartY=-11 StartZ=0 EndX=2.5 EndY=11 EndZ=0
    g2: LineSegment StartX=2.5 StartY=11 StartZ=0 EndX=-2.5 EndY=11 EndZ=0
    g3: LineSegment StartX=-2.5 StartY=11 StartZ=0 EndX=-2.5 EndY=-11 EndZ=0
    g4: GeomPoint [constr] X=0 Y=0 Z=0
  constraints (12):
    c: Coincident(g0,g1)
    c: Coincident(g1,g2)
    c: Coincident(g2,g3)
    c: Coincident(g3,g0)
    c: Horizontal(g0)
    c: Horizontal(g2)
    c: Vertical(g1)
    c: Vertical(g3)
    c: Symmetric(g2,g0,g4)
    c: Distance(g1,g3) = 5
    c: Distance(g0,g2) = 22
    c: Coincident(g4,g-1)
FEATURE [PartDesign::Pad] Pad007
  BaseFeature = -> Hole009
  Direction = (0,0,1)
  Length = 37
  Length2 = 10
  Profile = -> Sketch021
  ReferenceAxis = -> Sketch021 [N_Axis]
  Refine = true
  SideType = 0
  Suppressed = false
  Type = 0
  Type2 = 0
FEATURE [PartDesign::Fillet] Fillet001
  Base = -> Pad007 [Edge23,Edge21]
  BaseFeature = -> Pad007
  Radius = 3
  Refine = true
  SupportTransform = false
  Suppressed = false
  UseAllEdges = false
FEATURE [Sketcher::SketchObject] Sketch022
  ArcFitTolerance = 1e-06
  AttachmentSupport = -> [Fillet001]
  ExternalTypes = [0,0]
  FullyConstrained = true
  MakeInternals = false
  MapMode = 5
  Placement = pos=(-2.5,0,0) rot=(0.57735,-0.57735,-0.57735;2.0944rad)
  _ExternalGeoVersion = 1
  sketch-geometry (2):
    g0: ArcOfCircle CenterX=6.6e-13 CenterY=42 CenterZ=0 NormalX=0 NormalY=0 NormalZ=1 AngleXU=0 Radius=11 StartAngle=0 EndAngle=3.14159
    g1: LineSegment StartX=-11 StartY=42 StartZ=0 EndX=11 EndY=42 EndZ=0
  constraints (7):
    c: Coincident(g1,g0)
    c: Coincident(g1,g0)
    c: DistanceY(g-1,g0) = 42
    c: DistanceY(g-1,g0) = 42
    c: Distance(g0,g-2) = 11
    c: Distance(g0,g-2) = 11
    c: Distance(g0,g-1) = 31
FEATURE [PartDesign::Pad] Pad008
  BaseFeature = -> Fillet001
  Direction = (-1,0,0)
  Length = 5
  Length2 = 10
  Profile = -> Sketch022
  ReferenceAxis = -> Sketch022 [N_Axis]
  Refine = true
  Reversed = true
  SideType = 0
  Suppressed = false
  Type = 0
  Type2 = 0
FEATURE [Sketcher::SketchObject] Sketch023
  ArcFitTolerance = 1e-06
  AttachmentSupport = -> [Pad008]
  ExternalTypes = [0]
  FullyConstrained = true
  MakeInternals = false
  MapMode = 5
  Placement = pos=(2.5,0,0) rot=(0.57735,0.57735,0.57735;2.0944rad)
  _ExternalGeoVersion = 1
  sketch-geometry (8):
    g0: Circle CenterX=-6.87 CenterY=37.91 CenterZ=0 NormalX=0 NormalY=0 NormalZ=1 AngleXU=0 Radius=0.75
    g1: Circle CenterX=-7.75 CenterY=43.96 CenterZ=0 NormalX=0 NormalY=0 NormalZ=1 AngleXU=0 Radius=0.75
    g2: Circle CenterX=-4.1 CenterY=48.87 CenterZ=0 NormalX=0 NormalY=0 NormalZ=1 AngleXU=0 Radius=0.75
    g3: Circle CenterX=1.96 CenterY=49.75 CenterZ=0 NormalX=0 NormalY=0 NormalZ=1 AngleXU=0 Radius=0.75
    g4: Circle CenterX=6.87 CenterY=46.09 CenterZ=0 NormalX=0 NormalY=0 NormalZ=1 AngleXU=0 Radius=0.75
    g5: Circle CenterX=7.75 CenterY=40.04 CenterZ=0 NormalX=0 NormalY=0 NormalZ=1 AngleXU=0 Radius=0.75
    g6: Circle CenterX=4.1 CenterY=35.13 CenterZ=0 NormalX=0 NormalY=0 NormalZ=1 AngleXU=0 Radius=0.75
    g7: Circle CenterX=-1.97 CenterY=34.24 CenterZ=0 NormalX=0 NormalY=0 NormalZ=1 AngleXU=0 Radius=0.75
  constraints (24):
    c: Diameter(g0) = 1.5
    c: Distance(g0,g-2) = 6.87
    c: Distance(g0,g-1) = 37.91
    c: Equal(g0,g1)
    c: Equal(g1,g2)
    c: Equal(g2,g3)
    c: Equal(g3,g4)
    c: Equal(g4,g5)
    c: Equal(g5,g6)
    c: Equal(g6,g7)
    c: Distance(g1,g-2) = 7.75
    c: Distance(g2,g-2) = 4.1
    c: Distance(g3,g-2) = 1.96
    c: Distance(g4,g-2) = 6.87
    c: Distance(g5,g-2) = 7.75
    c: Distance(g6,g-2) = 4.1
    c: Distance(g7,g-2) = 1.97
    c: Distance(g7,g-1) = 34.24
    c: DistanceY(g-1,g1) = 43.96
    c: DistanceY(g-1,g2) = 48.87
    c: DistanceY(g-1,g3) = 49.75
    c: DistanceY(g-1,g4) = 46.09
    c: DistanceY(g-1,g5) = 40.04
    c: DistanceY(g-1,g6) = 35.13
FEATURE [PartDesign::Hole] Hole010
  BaseFeature = -> Pad008
  BaseProfileType = 7
  CustomThreadClearance = 0
  Depth = 5
  DepthType = 0
  Diameter = 2.552
  DrillForDepth = false
  DrillPoint = 1
  DrillPointAngle = 118
  HoleCutCountersinkAngle = 90
  HoleCutCustomValues = false
  HoleCutDepth = 0
  HoleCutDiameter = 0
  HoleCutType = 0
  ModelThread = false
  Profile = -> Sketch023
  Refine = true
  Suppressed = false
  Tapered = false
  TaperedAngle = 90
  ThreadClass = 0
  ThreadDepth = 5
  ThreadDepthType = 0
  ThreadDiameter = 2.2
  ThreadDirection = 0
  ThreadFit = 2
  ThreadSize = 7
  ThreadType = 1
  Threaded = false
  UseCustomThreadClearance = false
FEATURE [Sketcher::SketchObject] Sketch024
  ArcFitTolerance = 1e-06
  AttachmentSupport = -> [Hole010]
  ExternalTypes = [0,0]
  FullyConstrained = true
  MakeInternals = false
  MapMode = 5
  Placement = pos=(2.5,0,0) rot=(0.57735,0.57735,0.57735;2.0944rad)
  _ExternalGeoVersion = 1
  sketch-geometry (1):
    g0: Circle CenterX=0 CenterY=42 CenterZ=0 NormalX=0 NormalY=0 NormalZ=1 AngleXU=0 Radius=5.5
  constraints (3):
    c: Diameter(g0) = 11
    c: PointOnObject(g0,g-2)
    c: DistanceY(g-1,g0) = 42
FEATURE [PartDesign::Hole] Hole008
  BaseFeature = -> Hole010
  BaseProfileType = 7
  CustomThreadClearance = 0
  Depth = 2.5
  DepthType = 0
  Diameter = 9
  DrillForDepth = false
  DrillPoint = 1
  DrillPointAngle = 118
  HoleCutCountersinkAngle = 90
  HoleCutCustomValues = false
  HoleCutDepth = 0
  HoleCutDiameter = 0
  HoleCutType = 0
  ModelThread = false
  Profile = -> Sketch024
  Refine = true
  Suppressed = false
  Tapered = false
  TaperedAngle = 90
  ThreadClass = 0
  ThreadDepth = 2.5
  ThreadDepthType = 0
  ThreadDiameter = 8
  ThreadDirection = 0
  ThreadFit = 0
  ThreadSize = 16
  ThreadType = 1
  Threaded = false
  UseCustomThreadClearance = false
FEATURE [Sketcher::SketchObject] Sketch025
  ArcFitTolerance = 1e-06
  AttachmentSupport = -> [Hole008]
  ExternalTypes = [0]
  FullyConstrained = true
  MakeInternals = false
  MapMode = 5
  Placement = pos=(-2.5,0,0) rot=(0.57735,-0.57735,-0.57735;2.0944rad)
  _ExternalGeoVersion = 1
  sketch-geometry (1):
    g0: Circle CenterX=0 CenterY=41.6 CenterZ=0 NormalX=0 NormalY=0 NormalZ=1 AngleXU=0 Radius=1.1
  constraints (3):
    c: Diameter(g0) = 2.2
    c: PointOnObject(g0,g-2)
    c: DistanceY(g-1,g0) = 41.6
FEATURE [PartDesign::Hole] Hole011
  BaseFeature = -> Hole008
  BaseProfileType = 7
  CustomThreadClearance = 0
  Depth = 2.5
  DepthType = 0
  Diameter = 2.9
  DrillForDepth = false
  DrillPoint = 1
  DrillPointAngle = 118
  HoleCutCountersinkAngle = 90
  HoleCutCustomValues = false
  HoleCutDepth = 0
  HoleCutDiameter = 0
  HoleCutType = 0
  ModelThread = false
  Profile = -> Sketch025
  Refine = true
  Suppressed = false
  Tapered = false
  TaperedAngle = 90
  ThreadClass = 0
  ThreadDepth = 2.5
  ThreadDepthType = 0
  ThreadDiameter = 2.5
  ThreadDirection = 0
  ThreadFit = 0
  ThreadSize = 8
  ThreadType = 1
  Threaded = false
  UseCustomThreadClearance = false
FEATURE [PartDesign::Body] Body003  label="horn_holder001"
  AllowCompound = true
  Group = -> [Sketch019,Pad006,Sketch020,Hole009,Sketch021,Pad007,Fillet001,Sketch022,Pad008,Sketch023,Hole010,Sketch024,Hole008,Sketch025,Hole011]
  Origin = -> Origin015
  Tip = -> Hole011
FEATURE [Sketcher::SketchObject] Sketch026
  ArcFitTolerance = 1e-06
  AttachmentSupport = -> [Mirrored]
  ExternalTypes = [0]
  FullyConstrained = true
  MakeInternals = false
  MapMode = 5
  Placement = pos=(0,0,5) rot=(0,0,1;0rad)
  _ExternalGeoVersion = 1
  sketch-geometry (8):
    g0: ArcOfCircle CenterX=45 CenterY=-25 CenterZ=0 NormalX=0 NormalY=0 NormalZ=1 AngleXU=0 Radius=3 StartAngle=1.5708 EndAngle=4.71239
    g1: ArcOfCircle CenterX=105 CenterY=-25 CenterZ=0 NormalX=0 NormalY=0 NormalZ=1 AngleXU=0 Radius=3 StartAngle=4.71239 EndAngle=7.85398
    g2: LineSegment StartX=45 StartY=-22 StartZ=0 EndX=105 EndY=-22 EndZ=0
    g3: LineSegment StartX=45 StartY=-28 StartZ=0 EndX=105 EndY=-28 EndZ=0
    g4: ArcOfCircle CenterX=45 CenterY=25 CenterZ=0 NormalX=0 NormalY=0 NormalZ=1 AngleXU=0 Radius=3 StartAngle=1.5708 EndAngle=4.71239
    g5: ArcOfCircle CenterX=105 CenterY=25 CenterZ=0 NormalX=0 NormalY=0 NormalZ=1 AngleXU=0 Radius=3 StartAngle=4.71239 EndAngle=7.85398
    g6: LineSegment StartX=45 StartY=28 StartZ=0 EndX=105 EndY=28 EndZ=0
    g7: LineSegment StartX=45 StartY=22 StartZ=0 EndX=105 EndY=22 EndZ=0
  constraints (20):
    c: Tangent(g0,g2) = 1.5708
    c: Tangent(g0,g3) = -1.5708
    c: Tangent(g1,g2) = 1.5708
    c: Tangent(g1,g3) = -1.5708
    c: Equal(g0,g1)
    c: Distance(g0,g1) = 60
    c: Radius(g0) = 3
    c: Horizontal(g2)
    c: Distance(g-1,g2) = 22
    c: Distance(g0,g-2) = 45
    c: Tangent(g4,g6) = 1.5708
    c: Tangent(g4,g7) = -1.5708
    c: Tangent(g5,g6) = 1.5708
    c: Tangent(g5,g7) = -1.5708
    c: Equal(g4,g5)
    c: Distance(g4,g5) = 60
    c: Radius(g4) = 3
    c: Horizontal(g6)
    c: Distance(g-1,g7) = 22
    c: Distance(g4,g-2) = 45
FEATURE [PartDesign::Pocket] Pocket
  BaseFeature = -> Mirrored
  Direction = (0,0,-1)
  Length = 5
  Length2 = 5
  Profile = -> Sketch026
  ReferenceAxis = -> Sketch026 [N_Axis]
  Refine = true
  SideType = 0
  Suppressed = false
  Type = 0
  Type2 = 0
FEATURE [PartDesign::Mirrored] Mirrored001
  BaseFeature = -> Pocket
  MirrorPlane = -> Sketch026 [V_Axis]
  Originals = -> [Pocket]
  Refine = true
  Suppressed = false
  TransformMode = 0
FEATURE [PartDesign::Body] Body
  AllowCompound = true
  Group = -> [Sketch,Pad,Sketch001,Hole,Mirrored,Sketch026,Pocket,Mirrored001]
  Origin = -> Origin
  Tip = -> Mirrored001
FEATURE [TechDraw::DrawSVGTemplate] Template
  Height = 210
  Orientation = 1
  Template = <path>
  Width = 297
FEATURE [TechDraw::DrawProjGroupItem] View
  CoarseView = false
  Direction = (0,0,1)
  Focus = 100
  HardHidden = false
  IsoCount = 0
  IsoHidden = false
  IsoVisible = false
  LockPosition = false
  Perspective = false
  Rotation = 0
  RotationVector = (1,0,0)
  ScaleType = 0
  ScrubCount = 1
  SeamHidden = false
  SeamVisible = false
  SmoothHidden = false
  SmoothVisible = true
  Source = -> [Body]
  Type = 0
  X = 148.5
  XDirection = (1,0,0)
  Y = 105
FEATURE [TechDraw::DrawViewDimension] Dimension
  AngleOverride = false
  Arbitrary = false
  ArbitraryTolerances = false
  BoxCorners = (2) [(-114.3,-90,0),(114.3,90,0)]
  EqualTolerance = true
  ExtensionAngle = 0
  FormatSpec = %.2w
  FormatSpecOverTolerance = %+.2w
  FormatSpecUnderTolerance = %+.2w
  Inverted = false
  LineAngle = 0
  LockPosition = false
  MeasureType = 1
  OverTolerance = 0
  References2D = -> [View]
  Rotation = 0
  ScaleType = 0
  ShowUnits = false
  TheoreticalExact = false
  Type = 2
  UnderTolerance = 0
  UseActualArea = true
  X = -138.027
  Y = -5.66711
FEATURE [TechDraw::DrawViewDimension] Dimension001
  AngleOverride = false
  Arbitrary = false
  ArbitraryTolerances = false
  BoxCorners = (2) [(-114.3,-90,0),(114.3,90,0)]
  EqualTolerance = true
  ExtensionAngle = 0
  FormatSpec = %.2w
  FormatSpecOverTolerance = %+.2w
  FormatSpecUnderTolerance = %+.2w
  Inverted = false
  LineAngle = 0
  LockPosition = false
  MeasureType = 1
  OverTolerance = 0
  References2D = -> [View]
  Rotation = 0
  ScaleType = 0
  ShowUnits = false
  TheoreticalExact = false
  Type = 1
  UnderTolerance = 0
  UseActualArea = true
  X = -8.01384
  Y = 102.586
FEATURE [TechDraw::DrawPage] Page
  KeepUpdated = true
  NextBalloonIndex = 1
  ProjectionType = 0
  Template = -> Template
  Views = -> [View,Dimension,Dimension001]
FEATURE [App::Point] Origin017  label="Origin019"
  Role = Origin
FEATURE [PartDesign::ShapeBinder] CopyMirrored001
  TraceSupport = false
FEATURE [Sketcher::SketchObject] Sketch027
  ArcFitTolerance = 1e-06
  AttachmentSupport = -> [CopyMirrored001]
  ExternalTypes = [0]
  FullyConstrained = true
  MakeInternals = false
  MapMode = 5
  Placement = pos=(0,0,5) rot=(0,0,1;0rad)
  _ExternalGeoVersion = 1
  sketch-geometry (6):
    g0: LineSegment StartX=-50 StartY=50 StartZ=0 EndX=-50 EndY=-75 EndZ=0
    g1: LineSegment StartX=-43 StartY=-70 StartZ=0 EndX=-43 EndY=50 EndZ=0
    g2: LineSegment StartX=-43 StartY=50 StartZ=0 EndX=-50 EndY=50 EndZ=0
    g3: LineSegment StartX=-50 StartY=-75 StartZ=0 EndX=-35 EndY=-75 EndZ=0
    g4: LineSegment StartX=-35 StartY=-75 StartZ=0 EndX=-35 EndY=-70 EndZ=0
    g5: LineSegment StartX=-35 StartY=-70 StartZ=0 EndX=-43 EndY=-70 EndZ=0
  constraints (18):
    c: Coincident(g1,g2)
    c: Coincident(g2,g0)
    c: Vertical(g0)
    c: Horizontal(g2)
    c: Distance(g-2,g0) = 50
    c: Distance(g2,g2) = 7
    c: Coincident(g3,g4)
    c: Coincident(g4,g5)
    c: Horizontal(g3)
    c: Vertical(g4)
    c: Distance(g4,g3) = 15
    c: Coincident(g3,g0)
    c: Vertical(g1)
    c: Horizontal(g5)
    c: Coincident(g1,g5)
    c: Distance(g-1,g3) = 75
    c: Distance(g-1,g5) = 70
    c: Distance(g-1,g2) = 50
FEATURE [PartDesign::Pad] Pad009
  Direction = (0,0,1)
  Length = 15
  Length2 = 10
  Profile = -> Sketch027
  ReferenceAxis = -> Sketch027 [N_Axis]
  Refine = true
  SideType = 0
  Suppressed = false
  Type = 0
  Type2 = 0
FEATURE [Sketcher::SketchObject] Sketch028
  ArcFitTolerance = 1e-06
  AttachmentSupport = -> [Pad009]
  ExternalTypes = [0]
  FullyConstrained = true
  MakeInternals = false
  MapMode = 5
  Placement = pos=(0,0,5) rot=(1,0,0;3.14159rad)
  _ExternalGeoVersion = 1
  sketch-geometry (4):
    g0: LineSegment StartX=-50 StartY=12 StartZ=0 EndX=-78 EndY=12 EndZ=0
    g1: LineSegment StartX=-78 StartY=12 StartZ=0 EndX=-78 EndY=-12 EndZ=0
    g2: LineSegment StartX=-78 StartY=-12 StartZ=0 EndX=-50 EndY=-12 EndZ=0
    g3: LineSegment StartX=-50 StartY=-12 StartZ=0 EndX=-50 EndY=12 EndZ=0
  constraints (12):
    c: Coincident(g0,g1)
    c: Coincident(g1,g2)
    c: Coincident(g2,g3)
    c: Coincident(g3,g0)
    c: Horizontal(g0)
    c: Horizontal(g2)
    c: Vertical(g1)
    c: Vertical(g3)
    c: Distance(g1,g3) = 28
    c: Distance(g0,g2) = 24
    c: Distance(g-1,g2) = 12
    c: Distance(g-2,g3) = 50
FEATURE [PartDesign::Pad] Pad010
  BaseFeature = -> Pad009
  Direction = (0,0,-1)
  Length = 5
  Length2 = 10
  Profile = -> Sketch028
  ReferenceAxis = -> Sketch028 [N_Axis]
  Refine = true
  Reversed = true
  SideType = 0
  Suppressed = false
  Type = 0
  Type2 = 0
FEATURE [PartDesign::Fillet] Fillet002
  Base = -> Pad010 [Edge4,Edge3,Edge2]
  BaseFeature = -> Pad010
  Radius = 3
  Refine = true
  SupportTransform = false
  Suppressed = false
  UseAllEdges = false
FEATURE [PartDesign::Fillet] Fillet003
  Base = -> Fillet002 [Edge31,Edge34]
  BaseFeature = -> Fillet002
  Radius = 3
  Refine = true
  SupportTransform = false
  Suppressed = false
  UseAllEdges = false
FEATURE [Sketcher::SketchObject] Sketch029
  ArcFitTolerance = 1e-06
  AttachmentSupport = -> [Fillet003]
  ExternalTypes = [0]
  FullyConstrained = true
  MakeInternals = false
  MapMode = 5
  Placement = pos=(0,0,10) rot=(0,0,1;0rad)
  _ExternalGeoVersion = 1
  sketch-geometry (4):
    g0: Circle CenterX=-71.81 CenterY=7.5 CenterZ=0 NormalX=0 NormalY=0 NormalZ=1 AngleXU=0 Radius=1.5
    g1: Circle CenterX=-56.81 CenterY=7.5 CenterZ=0 NormalX=0 NormalY=0 NormalZ=1 AngleXU=0 Radius=1.5
    g2: Circle CenterX=-71.81 CenterY=-7.5 CenterZ=0 NormalX=0 NormalY=0 NormalZ=1 AngleXU=0 Radius=1.5
    g3: Circle CenterX=-56.81 CenterY=-7.5 CenterZ=0 NormalX=0 NormalY=0 NormalZ=1 AngleXU=0 Radius=1.5
  constraints (12):
    c: Diameter(g0) = 3
    c: Distance(g0,g-1) = 7.5
    c: Equal(g1,g0)
    c: Equal(g0,g2)
    c: Equal(g2,g3)
    c: Distance(g1,g-1) = 7.5
    c: DistanceX(g0,g1) = 15
    c: Distance(g2,g-1) = 7.5
    c: Distance(g3,g-1) = 7.5
    c: DistanceX(g2,g3) = 15
    c: DistanceX(g0,g-1) = 71.81
    c: DistanceX(g2,g-1) = 71.81
FEATURE [PartDesign::Hole] Hole012
  BaseFeature = -> Fillet003
  BaseProfileType = 7
  CustomThreadClearance = 0
  Depth = 5
  DepthType = 0
  Diameter = 3.6
  DrillForDepth = false
  DrillPoint = 0
  DrillPointAngle = 118
  HoleCutCountersinkAngle = 90
  HoleCutCustomValues = false
  HoleCutDepth = 0
  HoleCutDiameter = 0
  HoleCutType = 0
  ModelThread = false
  Profile = -> Sketch029
  Refine = true
  Suppressed = false
  Tapered = false
  TaperedAngle = 90
  ThreadClass = 0
  ThreadDepth = 5
  ThreadDepthType = 0
  ThreadDiameter = 3
  ThreadDirection = 0
  ThreadFit = 2
  ThreadSize = 9
  ThreadType = 1
  Threaded = false
  UseCustomThreadClearance = false
FEATURE [PartDesign::Fillet] Fillet004
  Base = -> Hole012 [Face12,Face10]
  BaseFeature = -> Hole012
  Radius = 1
  Refine = true
  SupportTransform = false
  Suppressed = false
  UseAllEdges = false
FEATURE [PartDesign::Fillet] Fillet005
  Base = -> Fillet004 [Edge30,Edge21]
  BaseFeature = -> Fillet004
  Radius = 2
  Refine = true
  SupportTransform = false
  Suppressed = false
  UseAllEdges = false
FEATURE [Sketcher::SketchObject] Sketch030
  ArcFitTolerance = 1e-06
  AttachmentSupport = -> [Fillet005]
  ExternalTypes = [0]
  FullyConstrained = true
  MakeInternals = false
  MapMode = 5
  Placement = pos=(0,0,5) rot=(1,0,0;3.14159rad)
  _ExternalGeoVersion = 1
  sketch-geometry (2):
    g0: Circle CenterX=-47 CenterY=25 CenterZ=0 NormalX=0 NormalY=0 NormalZ=1 AngleXU=0 Radius=2
    g1: Circle CenterX=-47 CenterY=-25 CenterZ=0 NormalX=0 NormalY=0 NormalZ=1 AngleXU=0 Radius=2
  constraints (6):
    c: Distance(g0,g-1) = 25
    c: Distance(g0,g-2) = 47
    c: Diameter(g0) = 4
    c: Equal(g1,g0)
    c: Distance(g1,g-1) = 25
    c: DistanceX(g1,g-1) = 47
FEATURE [PartDesign::Pad] Pad011
  BaseFeature = -> Fillet005
  Direction = (0,0,-1)
  Length = 5
  Length2 = 10
  Profile = -> Sketch030
  ReferenceAxis = -> Sketch030 [N_Axis]
  Refine = true
  SideType = 0
  Suppressed = false
  Type = 0
  Type2 = 0
FEATURE [PartDesign::Body] Body004  label="Body001"
  AllowCompound = true
  Group = -> [CopyMirrored001,Sketch027,Pad009,Sketch028,Pad010,Fillet002,Fillet003,Sketch029,Hole012,Fillet004,Fillet005,Sketch030,Pad011]
  Origin = -> Origin016
  Tip = -> Pad011
FEATURE [App::Point] Origin019  label="Origin021"
  Role = Origin
FEATURE [PartDesign::ShapeBinder] CopyMirrored002
  TraceSupport = false
FEATURE [Sketcher::SketchObject] Sketch031
  ArcFitTolerance = 1e-06
  AttachmentSupport = -> [CopyMirrored002]
  ExternalTypes = [0]
  FullyConstrained = true
  MakeInternals = false
  MapMode = 5
  Placement = pos=(0,0,5) rot=(0,0,1;0rad)
  _ExternalGeoVersion = 1
  sketch-geometry (6):
    g0: LineSegment StartX=55 StartY=50 StartZ=0 EndX=48 EndY=50 EndZ=0
    g1: LineSegment StartX=48 StartY=50 StartZ=0 EndX=48 EndY=-70 EndZ=0
    g2: LineSegment StartX=55 StartY=-75 StartZ=0 EndX=55 EndY=50 EndZ=0
    g3: LineSegment StartX=48 StartY=-70 StartZ=0 EndX=40 EndY=-70 EndZ=0
    g4: LineSegment StartX=40 StartY=-70 StartZ=0 EndX=40 EndY=-75 EndZ=0
    g5: LineSegment StartX=40 StartY=-75 StartZ=0 EndX=55 EndY=-75 EndZ=0
  constraints (18):
    c: Coincident(g0,g1)
    c: Coincident(g2,g0)
    c: Horizontal(g0)
    c: Vertical(g2)
    c: Distance(g1,g2) = 7
    c: Coincident(g3,g4)
    c: Coincident(g4,g5)
    c: Vertical(g4)
    c: Horizontal(g5)
    c: Distance(g5,g4) = 15
    c: Coincident(g5,g2)
    c: Vertical(g1)
    c: Horizontal(g3)
    c: Coincident(g1,g3)
    c: Distance(g-1,g0) = 50
    c: Distance(g-1,g5) = 75
    c: Distance(g-2,g2) = 55
    c: Distance(g-1,g3) = 70
FEATURE [PartDesign::Pad] Pad012
  Direction = (0,0,1)
  Length = 15
  Length2 = 10
  Profile = -> Sketch031
  ReferenceAxis = -> Sketch031 [N_Axis]
  Refine = true
  SideType = 0
  Suppressed = false
  Type = 0
  Type2 = 0
FEATURE [PartDesign::Fillet] Fillet006
  Base = -> Pad012 [Face3,Face2]
  BaseFeature = -> Pad012
  Radius = 1
  Refine = true
  SupportTransform = false
  Suppressed = false
  UseAllEdges = false
FEATURE [PartDesign::Fillet] Fillet007
  Base = -> Fillet006 [Edge14,Edge3]
  BaseFeature = -> Fillet006
  Radius = 2
  Refine = true
  SupportTransform = false
  Suppressed = false
  UseAllEdges = false
FEATURE [Sketcher::SketchObject] Sketch032
  ArcFitTolerance = 1e-06
  AttachmentSupport = -> [Fillet007]
  ExternalTypes = [0]
  FullyConstrained = true
  MakeInternals = false
  MapMode = 5
  Placement = pos=(0,0,5) rot=(1,0,0;3.14159rad)
  _ExternalGeoVersion = 1
  sketch-geometry (8):
    g0: LineSegment StartX=55 StartY=33 StartZ=0 EndX=55 EndY=17 EndZ=0
    g1: LineSegment StartX=55 StartY=17 StartZ=0 EndX=90 EndY=17 EndZ=0
    g2: LineSegment StartX=90 StartY=17 StartZ=0 EndX=90 EndY=33 EndZ=0
    g3: LineSegment StartX=90 StartY=33 StartZ=0 EndX=55 EndY=33 EndZ=0
    g4: LineSegment StartX=55 StartY=-17 StartZ=0 EndX=55 EndY=-33 EndZ=0
    g5: LineSegment StartX=55 StartY=-33 StartZ=0 EndX=90 EndY=-33 EndZ=0
    g6: LineSegment StartX=90 StartY=-33 StartZ=0 EndX=90 EndY=-17 EndZ=0
    g7: LineSegment StartX=90 StartY=-17 StartZ=0 EndX=55 EndY=-17 EndZ=0
  constraints (24):
    c: Coincident(g0,g1)
    c: Coincident(g1,g2)
    c: Coincident(g2,g3)
    c: Coincident(g3,g0)
    c: Vertical(g0)
    c: Vertical(g2)
    c: Horizontal(g1)
    c: Horizontal(g3)
    c: Distance(g0,g2) = 35
    c: Distance(g1,g3) = 16
    c: Coincident(g4,g5)
    c: Coincident(g5,g6)
    c: Coincident(g6,g7)
    c: Coincident(g7,g4)
    c: Vertical(g4)
    c: Vertical(g6)
    c: Horizontal(g5)
    c: Horizontal(g7)
    c: Distance(g4,g6) = 35
    c: Distance(g5,g7) = 16
    c: Distance(g-1,g1) = 17
    c: Distance(g-1,g7) = 17
    c: Distance(g-2,g0) = 55
    c: Distance(g-2,g4) = 55
FEATURE [PartDesign::Pad] Pad013
  BaseFeature = -> Fillet007
  Direction = (0,0,-1)
  Length = 5
  Length2 = 10
  Profile = -> Sketch032
  ReferenceAxis = -> Sketch032 [N_Axis]
  Refine = true
  Reversed = true
  SideType = 0
  Suppressed = false
  Type = 0
  Type2 = 0
FEATURE [PartDesign::Fillet] Fillet008
  Base = -> Pad013 [Edge23,Edge22,Edge24,Edge26,Edge27,Edge28]
  BaseFeature = -> Pad013
  Radius = 3
  Refine = true
  SupportTransform = false
  Suppressed = false
  UseAllEdges = false
FEATURE [PartDesign::Fillet] Fillet009
  Base = -> Fillet008 [Edge68,Edge66,Edge54,Edge51]
  BaseFeature = -> Fillet008
  Radius = 7
  Refine = true
  SupportTransform = false
  Suppressed = false
  UseAllEdges = false
FEATURE [Sketcher::SketchObject] Sketch033
  ArcFitTolerance = 1e-06
  AttachmentSupport = -> [Fillet009]
  ExternalGeometry = -> [Fillet009]
  ExternalTypes = [0]
  FullyConstrained = true
  MakeInternals = false
  MapMode = 5
  Placement = pos=(0,0,10) rot=(0,0,1;0rad)
  _ExternalGeoVersion = 1
  sketch-geometry (2):
    g0: Circle CenterX=80 CenterY=25 CenterZ=0 NormalX=0 NormalY=0 NormalZ=1 AngleXU=0 Radius=2.5
    g1: Circle CenterX=80 CenterY=-25 CenterZ=0 NormalX=0 NormalY=0 NormalZ=1 AngleXU=0 Radius=2.5
  constraints (6):
    c: Diameter(g0) = 5
    c: Distance(g0,g-1) = 25
    c: Distance(g0,g-2) = 80
    c: Equal(g0,g1)
    c: Distance(g1,g-1) = 25
    c: Distance(g1,g-2) = 80
FEATURE [PartDesign::Hole] Hole013
  BaseFeature = -> Fillet009
  BaseProfileType = 7
  CustomThreadClearance = 0
  Depth = 5
  DepthType = 0
  Diameter = 5.8
  DrillForDepth = false
  DrillPoint = 0
  DrillPointAngle = 118
  HoleCutCountersinkAngle = 90
  HoleCutCustomValues = false
  HoleCutDepth = 2.5
  HoleCutDiameter = 8
  HoleCutType = 1
  ModelThread = false
  Profile = -> Sketch033
  Refine = true
  Suppressed = false
  Tapered = false
  TaperedAngle = 90
  ThreadClass = 0
  ThreadDepth = 5
  ThreadDepthType = 0
  ThreadDiameter = 5
  ThreadDirection = 0
  ThreadFit = 2
  ThreadSize = 13
  ThreadType = 1
  Threaded = false
  UseCustomThreadClearance = false
FEATURE [Sketcher::SketchObject] Sketch034
  ArcFitTolerance = 1e-06
  AttachmentSupport = -> [Hole013]
  ExternalTypes = [0]
  FullyConstrained = true
  MakeInternals = false
  MapMode = 5
  Placement = pos=(0,0,5) rot=(1,0,0;3.14159rad)
  _ExternalGeoVersion = 1
  sketch-geometry (2):
    g0: Circle CenterX=52 CenterY=25 CenterZ=0 NormalX=0 NormalY=0 NormalZ=1 AngleXU=0 Radius=2
    g1: Circle CenterX=52 CenterY=-25 CenterZ=0 NormalX=0 NormalY=0 NormalZ=1 AngleXU=0 Radius=2
  constraints (6):
    c: Diameter(g0) = 4
    c: Distance(g0,g-2) = 52
    c: Distance(g0,g-1) = 25
    c: Equal(g1,g0)
    c: Distance(g1,g-2) = 52
    c: Distance(g1,g-1) = 25
FEATURE [PartDesign::Pad] Pad014
  BaseFeature = -> Hole013
  Direction = (0,0,-1)
  Length = 5
  Length2 = 10
  Profile = -> Sketch034
  ReferenceAxis = -> Sketch034 [N_Axis]
  Refine = true
  SideType = 0
  Suppressed = false
  Type = 0
  Type2 = 0
FEATURE [PartDesign::Body] Body005  label="Body002"
  AllowCompound = true
  Group = -> [CopyMirrored002,Sketch031,Pad012,Fillet006,Fillet007,Sketch032,Pad013,Fillet008,Fillet009,Sketch033,Hole013,Sketch034,Pad014]
  Origin = -> Origin018
  Tip = -> Pad014
note: 1 file-system path scrubbed to <path> (originals preserved in the JSON sidecar)
